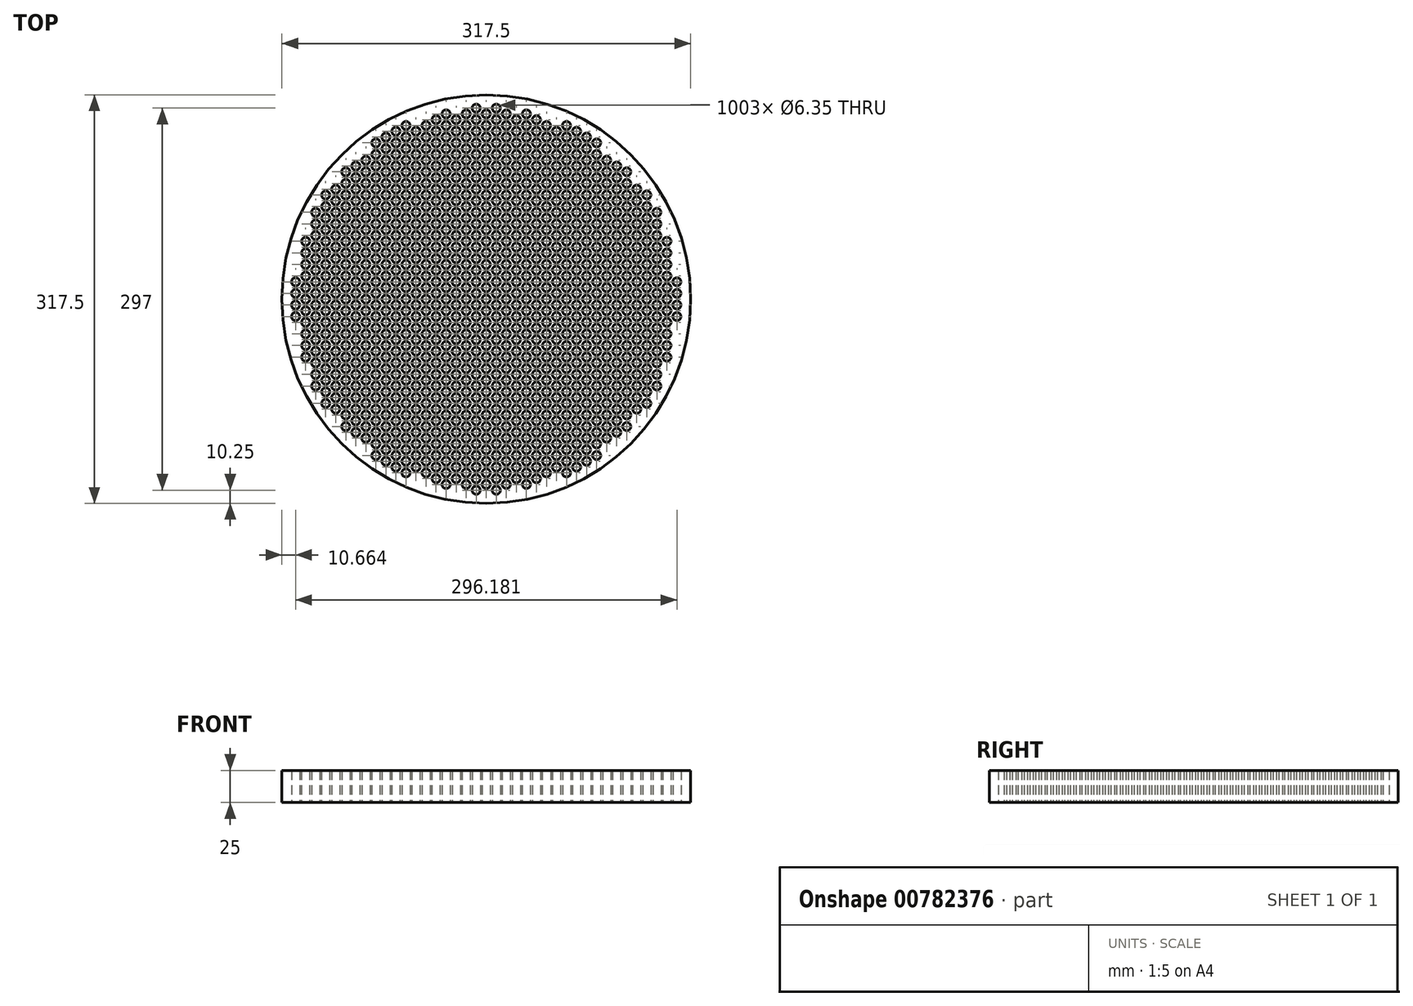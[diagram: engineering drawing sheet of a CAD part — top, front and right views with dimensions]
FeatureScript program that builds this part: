
annotation { "Feature Type Name" : "Feature", "Feature Type Description" : "" }
export const myFeature = defineFeature(function(context is Context, id is Id, definition is map)
    precondition{}
    {
        {
            var Q0;
            Q0=qCreatedBy(makeId("Top.planeOp"),FACE);
            var sketch = newSketch(context, id + "F0", { "sketchPlane" : qUnion([Q0])});
            skLineSegment(sketch, "E0.bottom", {"start": v(158.75, -158.75) * mm, "end": v(-158.75, -158.75) * mm});
            skLineSegment(sketch, "E0.top", {"start": v(158.75, 158.75) * mm, "end": v(-158.75, 158.75) * mm});
            skLineSegment(sketch, "E0.left", {"start": v(158.75, -158.75) * mm, "end": v(158.75, 158.75) * mm});
            skLineSegment(sketch, "E0.right", {"start": v(-158.75, -158.75) * mm, "end": v(-158.75, 158.75) * mm});
            skPoint(sketch, "E0.middle", {"position": v(0, 0) * mm});
            skCircle(sketch, "E1", {"center": v(-158.75, -158.75) * mm, "radius": 3.18 * mm});
            skCircle(sketch, "E2", {"center": v(-158.75, -149.75) * mm, "radius": 3.18 * mm});
            skCircle(sketch, "E3", {"center": v(-150.96, -154.25) * mm, "radius": 3.18 * mm});
            skCircle(sketch, "E4", {"center": v(-150.96, -145.25) * mm, "radius": 3.18 * mm});
            skCircle(sketch, "E5.0.1.0", {"center": v(-150.96, -127.25) * mm, "radius": 3.18 * mm});
            skCircle(sketch, "E5.0.1.1", {"center": v(-158.75, -140.75) * mm, "radius": 3.18 * mm});
            skCircle(sketch, "E5.0.1.2", {"center": v(-150.96, -136.25) * mm, "radius": 3.18 * mm});
            skCircle(sketch, "E5.0.1.3", {"center": v(-158.75, -131.75) * mm, "radius": 3.18 * mm});
            skCircle(sketch, "E5.0.2.0", {"center": v(-150.96, -109.25) * mm, "radius": 3.18 * mm});
            skCircle(sketch, "E5.0.2.1", {"center": v(-158.75, -122.75) * mm, "radius": 3.18 * mm});
            skCircle(sketch, "E5.0.2.2", {"center": v(-150.96, -118.25) * mm, "radius": 3.18 * mm});
            skCircle(sketch, "E5.0.2.3", {"center": v(-158.75, -113.75) * mm, "radius": 3.18 * mm});
            skCircle(sketch, "E5.0.3.0", {"center": v(-150.96, -91.25) * mm, "radius": 3.18 * mm});
            skCircle(sketch, "E5.0.3.1", {"center": v(-158.75, -104.75) * mm, "radius": 3.18 * mm});
            skCircle(sketch, "E5.0.3.2", {"center": v(-150.96, -100.25) * mm, "radius": 3.18 * mm});
            skCircle(sketch, "E5.0.3.3", {"center": v(-158.75, -95.75) * mm, "radius": 3.18 * mm});
            skCircle(sketch, "E5.0.4.0", {"center": v(-150.96, -73.25) * mm, "radius": 3.18 * mm});
            skCircle(sketch, "E5.0.4.1", {"center": v(-158.75, -86.75) * mm, "radius": 3.18 * mm});
            skCircle(sketch, "E5.0.4.2", {"center": v(-150.96, -82.25) * mm, "radius": 3.18 * mm});
            skCircle(sketch, "E5.0.4.3", {"center": v(-158.75, -77.75) * mm, "radius": 3.18 * mm});
            skCircle(sketch, "E5.0.5.0", {"center": v(-150.96, -55.25) * mm, "radius": 3.18 * mm});
            skCircle(sketch, "E5.0.5.1", {"center": v(-158.75, -68.75) * mm, "radius": 3.18 * mm});
            skCircle(sketch, "E5.0.5.2", {"center": v(-150.96, -64.25) * mm, "radius": 3.18 * mm});
            skCircle(sketch, "E5.0.5.3", {"center": v(-158.75, -59.75) * mm, "radius": 3.18 * mm});
            skCircle(sketch, "E5.0.6.0", {"center": v(-150.96, -37.25) * mm, "radius": 3.18 * mm});
            skCircle(sketch, "E5.0.6.1", {"center": v(-158.75, -50.75) * mm, "radius": 3.18 * mm});
            skCircle(sketch, "E5.0.6.2", {"center": v(-150.96, -46.25) * mm, "radius": 3.18 * mm});
            skCircle(sketch, "E5.0.6.3", {"center": v(-158.75, -41.75) * mm, "radius": 3.18 * mm});
            skCircle(sketch, "E5.0.7.0", {"center": v(-150.96, -19.25) * mm, "radius": 3.18 * mm});
            skCircle(sketch, "E5.0.7.1", {"center": v(-158.75, -32.75) * mm, "radius": 3.18 * mm});
            skCircle(sketch, "E5.0.7.2", {"center": v(-150.96, -28.25) * mm, "radius": 3.18 * mm});
            skCircle(sketch, "E5.0.7.3", {"center": v(-158.75, -23.75) * mm, "radius": 3.18 * mm});
            skCircle(sketch, "E5.0.8.0", {"center": v(-150.96, -1.25) * mm, "radius": 3.18 * mm});
            skCircle(sketch, "E5.0.8.1", {"center": v(-158.75, -14.75) * mm, "radius": 3.18 * mm});
            skCircle(sketch, "E5.0.8.2", {"center": v(-150.96, -10.25) * mm, "radius": 3.18 * mm});
            skCircle(sketch, "E5.0.8.3", {"center": v(-158.75, -5.75) * mm, "radius": 3.18 * mm});
            skCircle(sketch, "E5.0.9.0", {"center": v(-150.96, 16.75) * mm, "radius": 3.18 * mm});
            skCircle(sketch, "E5.0.9.1", {"center": v(-158.75, 3.25) * mm, "radius": 3.18 * mm});
            skCircle(sketch, "E5.0.9.2", {"center": v(-150.96, 7.75) * mm, "radius": 3.18 * mm});
            skCircle(sketch, "E5.0.9.3", {"center": v(-158.75, 12.25) * mm, "radius": 3.18 * mm});
            skCircle(sketch, "E5.0.10.0", {"center": v(-150.96, 34.75) * mm, "radius": 3.18 * mm});
            skCircle(sketch, "E5.0.10.1", {"center": v(-158.75, 21.25) * mm, "radius": 3.18 * mm});
            skCircle(sketch, "E5.0.10.2", {"center": v(-150.96, 25.75) * mm, "radius": 3.18 * mm});
            skCircle(sketch, "E5.0.10.3", {"center": v(-158.75, 30.25) * mm, "radius": 3.18 * mm});
            skCircle(sketch, "E5.0.11.0", {"center": v(-150.96, 52.75) * mm, "radius": 3.18 * mm});
            skCircle(sketch, "E5.0.11.1", {"center": v(-158.75, 39.25) * mm, "radius": 3.18 * mm});
            skCircle(sketch, "E5.0.11.2", {"center": v(-150.96, 43.75) * mm, "radius": 3.18 * mm});
            skCircle(sketch, "E5.0.11.3", {"center": v(-158.75, 48.25) * mm, "radius": 3.18 * mm});
            skCircle(sketch, "E5.0.12.0", {"center": v(-150.96, 70.75) * mm, "radius": 3.18 * mm});
            skCircle(sketch, "E5.0.12.1", {"center": v(-158.75, 57.25) * mm, "radius": 3.18 * mm});
            skCircle(sketch, "E5.0.12.2", {"center": v(-150.96, 61.75) * mm, "radius": 3.18 * mm});
            skCircle(sketch, "E5.0.12.3", {"center": v(-158.75, 66.25) * mm, "radius": 3.18 * mm});
            skCircle(sketch, "E5.0.13.0", {"center": v(-150.96, 88.75) * mm, "radius": 3.18 * mm});
            skCircle(sketch, "E5.0.13.1", {"center": v(-158.75, 75.25) * mm, "radius": 3.18 * mm});
            skCircle(sketch, "E5.0.13.2", {"center": v(-150.96, 79.75) * mm, "radius": 3.18 * mm});
            skCircle(sketch, "E5.0.13.3", {"center": v(-158.75, 84.25) * mm, "radius": 3.18 * mm});
            skCircle(sketch, "E5.0.14.0", {"center": v(-150.96, 106.75) * mm, "radius": 3.18 * mm});
            skCircle(sketch, "E5.0.14.1", {"center": v(-158.75, 93.25) * mm, "radius": 3.18 * mm});
            skCircle(sketch, "E5.0.14.2", {"center": v(-150.96, 97.75) * mm, "radius": 3.18 * mm});
            skCircle(sketch, "E5.0.14.3", {"center": v(-158.75, 102.25) * mm, "radius": 3.18 * mm});
            skCircle(sketch, "E5.0.15.0", {"center": v(-150.96, 124.75) * mm, "radius": 3.18 * mm});
            skCircle(sketch, "E5.0.15.1", {"center": v(-158.75, 111.25) * mm, "radius": 3.18 * mm});
            skCircle(sketch, "E5.0.15.2", {"center": v(-150.96, 115.75) * mm, "radius": 3.18 * mm});
            skCircle(sketch, "E5.0.15.3", {"center": v(-158.75, 120.25) * mm, "radius": 3.18 * mm});
            skCircle(sketch, "E5.0.16.0", {"center": v(-150.96, 142.75) * mm, "radius": 3.18 * mm});
            skCircle(sketch, "E5.0.16.1", {"center": v(-158.75, 129.25) * mm, "radius": 3.18 * mm});
            skCircle(sketch, "E5.0.16.2", {"center": v(-150.96, 133.75) * mm, "radius": 3.18 * mm});
            skCircle(sketch, "E5.0.16.3", {"center": v(-158.75, 138.25) * mm, "radius": 3.18 * mm});
            skCircle(sketch, "E5.0.17.0", {"center": v(-150.96, 160.75) * mm, "radius": 3.18 * mm});
            skCircle(sketch, "E5.0.17.1", {"center": v(-158.75, 147.25) * mm, "radius": 3.18 * mm});
            skCircle(sketch, "E5.0.17.2", {"center": v(-150.96, 151.75) * mm, "radius": 3.18 * mm});
            skCircle(sketch, "E5.0.17.3", {"center": v(-158.75, 156.25) * mm, "radius": 3.18 * mm});
            skCircle(sketch, "E5.1.0.0", {"center": v(-135.37, -145.25) * mm, "radius": 3.18 * mm});
            skCircle(sketch, "E5.1.0.1", {"center": v(-143.16, -158.75) * mm, "radius": 3.18 * mm});
            skCircle(sketch, "E5.1.0.2", {"center": v(-135.37, -154.25) * mm, "radius": 3.18 * mm});
            skCircle(sketch, "E5.1.0.3", {"center": v(-143.16, -149.75) * mm, "radius": 3.18 * mm});
            skCircle(sketch, "E5.1.1.0", {"center": v(-135.37, -127.25) * mm, "radius": 3.18 * mm});
            skCircle(sketch, "E5.1.1.1", {"center": v(-143.16, -140.75) * mm, "radius": 3.18 * mm});
            skCircle(sketch, "E5.1.1.2", {"center": v(-135.37, -136.25) * mm, "radius": 3.18 * mm});
            skCircle(sketch, "E5.1.1.3", {"center": v(-143.16, -131.75) * mm, "radius": 3.18 * mm});
            skCircle(sketch, "E5.1.2.0", {"center": v(-135.37, -109.25) * mm, "radius": 3.18 * mm});
            skCircle(sketch, "E5.1.2.1", {"center": v(-143.16, -122.75) * mm, "radius": 3.18 * mm});
            skCircle(sketch, "E5.1.2.2", {"center": v(-135.37, -118.25) * mm, "radius": 3.18 * mm});
            skCircle(sketch, "E5.1.2.3", {"center": v(-143.16, -113.75) * mm, "radius": 3.18 * mm});
            skCircle(sketch, "E5.1.3.0", {"center": v(-135.37, -91.25) * mm, "radius": 3.18 * mm});
            skCircle(sketch, "E5.1.3.1", {"center": v(-143.16, -104.75) * mm, "radius": 3.18 * mm});
            skCircle(sketch, "E5.1.3.2", {"center": v(-135.37, -100.25) * mm, "radius": 3.18 * mm});
            skCircle(sketch, "E5.1.3.3", {"center": v(-143.16, -95.75) * mm, "radius": 3.18 * mm});
            skCircle(sketch, "E5.1.4.0", {"center": v(-135.37, -73.25) * mm, "radius": 3.18 * mm});
            skCircle(sketch, "E5.1.4.1", {"center": v(-143.16, -86.75) * mm, "radius": 3.18 * mm});
            skCircle(sketch, "E5.1.4.2", {"center": v(-135.37, -82.25) * mm, "radius": 3.18 * mm});
            skCircle(sketch, "E5.1.4.3", {"center": v(-143.16, -77.75) * mm, "radius": 3.18 * mm});
            skCircle(sketch, "E5.1.5.0", {"center": v(-135.37, -55.25) * mm, "radius": 3.18 * mm});
            skCircle(sketch, "E5.1.5.1", {"center": v(-143.16, -68.75) * mm, "radius": 3.18 * mm});
            skCircle(sketch, "E5.1.5.2", {"center": v(-135.37, -64.25) * mm, "radius": 3.18 * mm});
            skCircle(sketch, "E5.1.5.3", {"center": v(-143.16, -59.75) * mm, "radius": 3.18 * mm});
            skCircle(sketch, "E5.1.6.0", {"center": v(-135.37, -37.25) * mm, "radius": 3.18 * mm});
            skCircle(sketch, "E5.1.6.1", {"center": v(-143.16, -50.75) * mm, "radius": 3.18 * mm});
            skCircle(sketch, "E5.1.6.2", {"center": v(-135.37, -46.25) * mm, "radius": 3.18 * mm});
            skCircle(sketch, "E5.1.6.3", {"center": v(-143.16, -41.75) * mm, "radius": 3.18 * mm});
            skCircle(sketch, "E5.1.7.0", {"center": v(-135.37, -19.25) * mm, "radius": 3.18 * mm});
            skCircle(sketch, "E5.1.7.1", {"center": v(-143.16, -32.75) * mm, "radius": 3.18 * mm});
            skCircle(sketch, "E5.1.7.2", {"center": v(-135.37, -28.25) * mm, "radius": 3.18 * mm});
            skCircle(sketch, "E5.1.7.3", {"center": v(-143.16, -23.75) * mm, "radius": 3.18 * mm});
            skCircle(sketch, "E5.1.8.0", {"center": v(-135.37, -1.25) * mm, "radius": 3.18 * mm});
            skCircle(sketch, "E5.1.8.1", {"center": v(-143.16, -14.75) * mm, "radius": 3.18 * mm});
            skCircle(sketch, "E5.1.8.2", {"center": v(-135.37, -10.25) * mm, "radius": 3.18 * mm});
            skCircle(sketch, "E5.1.8.3", {"center": v(-143.16, -5.75) * mm, "radius": 3.18 * mm});
            skCircle(sketch, "E5.1.9.0", {"center": v(-135.37, 16.75) * mm, "radius": 3.18 * mm});
            skCircle(sketch, "E5.1.9.1", {"center": v(-143.16, 3.25) * mm, "radius": 3.18 * mm});
            skCircle(sketch, "E5.1.9.2", {"center": v(-135.37, 7.75) * mm, "radius": 3.18 * mm});
            skCircle(sketch, "E5.1.9.3", {"center": v(-143.16, 12.25) * mm, "radius": 3.18 * mm});
            skCircle(sketch, "E5.1.10.0", {"center": v(-135.37, 34.75) * mm, "radius": 3.18 * mm});
            skCircle(sketch, "E5.1.10.1", {"center": v(-143.16, 21.25) * mm, "radius": 3.18 * mm});
            skCircle(sketch, "E5.1.10.2", {"center": v(-135.37, 25.75) * mm, "radius": 3.18 * mm});
            skCircle(sketch, "E5.1.10.3", {"center": v(-143.16, 30.25) * mm, "radius": 3.18 * mm});
            skCircle(sketch, "E5.1.11.0", {"center": v(-135.37, 52.75) * mm, "radius": 3.18 * mm});
            skCircle(sketch, "E5.1.11.1", {"center": v(-143.16, 39.25) * mm, "radius": 3.18 * mm});
            skCircle(sketch, "E5.1.11.2", {"center": v(-135.37, 43.75) * mm, "radius": 3.18 * mm});
            skCircle(sketch, "E5.1.11.3", {"center": v(-143.16, 48.25) * mm, "radius": 3.18 * mm});
            skCircle(sketch, "E5.1.12.0", {"center": v(-135.37, 70.75) * mm, "radius": 3.18 * mm});
            skCircle(sketch, "E5.1.12.1", {"center": v(-143.16, 57.25) * mm, "radius": 3.18 * mm});
            skCircle(sketch, "E5.1.12.2", {"center": v(-135.37, 61.75) * mm, "radius": 3.18 * mm});
            skCircle(sketch, "E5.1.12.3", {"center": v(-143.16, 66.25) * mm, "radius": 3.18 * mm});
            skCircle(sketch, "E5.1.13.0", {"center": v(-135.37, 88.75) * mm, "radius": 3.18 * mm});
            skCircle(sketch, "E5.1.13.1", {"center": v(-143.16, 75.25) * mm, "radius": 3.18 * mm});
            skCircle(sketch, "E5.1.13.2", {"center": v(-135.37, 79.75) * mm, "radius": 3.18 * mm});
            skCircle(sketch, "E5.1.13.3", {"center": v(-143.16, 84.25) * mm, "radius": 3.18 * mm});
            skCircle(sketch, "E5.1.14.0", {"center": v(-135.37, 106.75) * mm, "radius": 3.18 * mm});
            skCircle(sketch, "E5.1.14.1", {"center": v(-143.16, 93.25) * mm, "radius": 3.18 * mm});
            skCircle(sketch, "E5.1.14.2", {"center": v(-135.37, 97.75) * mm, "radius": 3.18 * mm});
            skCircle(sketch, "E5.1.14.3", {"center": v(-143.16, 102.25) * mm, "radius": 3.18 * mm});
            skCircle(sketch, "E5.1.15.0", {"center": v(-135.37, 124.75) * mm, "radius": 3.18 * mm});
            skCircle(sketch, "E5.1.15.1", {"center": v(-143.16, 111.25) * mm, "radius": 3.18 * mm});
            skCircle(sketch, "E5.1.15.2", {"center": v(-135.37, 115.75) * mm, "radius": 3.18 * mm});
            skCircle(sketch, "E5.1.15.3", {"center": v(-143.16, 120.25) * mm, "radius": 3.18 * mm});
            skCircle(sketch, "E5.1.16.0", {"center": v(-135.37, 142.75) * mm, "radius": 3.18 * mm});
            skCircle(sketch, "E5.1.16.1", {"center": v(-143.16, 129.25) * mm, "radius": 3.18 * mm});
            skCircle(sketch, "E5.1.16.2", {"center": v(-135.37, 133.75) * mm, "radius": 3.18 * mm});
            skCircle(sketch, "E5.1.16.3", {"center": v(-143.16, 138.25) * mm, "radius": 3.18 * mm});
            skCircle(sketch, "E5.1.17.0", {"center": v(-135.37, 160.75) * mm, "radius": 3.18 * mm});
            skCircle(sketch, "E5.1.17.1", {"center": v(-143.16, 147.25) * mm, "radius": 3.18 * mm});
            skCircle(sketch, "E5.1.17.2", {"center": v(-135.37, 151.75) * mm, "radius": 3.18 * mm});
            skCircle(sketch, "E5.1.17.3", {"center": v(-143.16, 156.25) * mm, "radius": 3.18 * mm});
            skCircle(sketch, "E5.2.0.0", {"center": v(-119.78, -145.25) * mm, "radius": 3.18 * mm});
            skCircle(sketch, "E5.2.0.1", {"center": v(-127.57, -158.75) * mm, "radius": 3.18 * mm});
            skCircle(sketch, "E5.2.0.2", {"center": v(-119.78, -154.25) * mm, "radius": 3.18 * mm});
            skCircle(sketch, "E5.2.0.3", {"center": v(-127.57, -149.75) * mm, "radius": 3.18 * mm});
            skCircle(sketch, "E5.2.1.0", {"center": v(-119.78, -127.25) * mm, "radius": 3.18 * mm});
            skCircle(sketch, "E5.2.1.1", {"center": v(-127.57, -140.75) * mm, "radius": 3.18 * mm});
            skCircle(sketch, "E5.2.1.2", {"center": v(-119.78, -136.25) * mm, "radius": 3.18 * mm});
            skCircle(sketch, "E5.2.1.3", {"center": v(-127.57, -131.75) * mm, "radius": 3.18 * mm});
            skCircle(sketch, "E5.2.2.0", {"center": v(-119.78, -109.25) * mm, "radius": 3.18 * mm});
            skCircle(sketch, "E5.2.2.1", {"center": v(-127.57, -122.75) * mm, "radius": 3.18 * mm});
            skCircle(sketch, "E5.2.2.2", {"center": v(-119.78, -118.25) * mm, "radius": 3.18 * mm});
            skCircle(sketch, "E5.2.2.3", {"center": v(-127.57, -113.75) * mm, "radius": 3.18 * mm});
            skCircle(sketch, "E5.2.3.0", {"center": v(-119.78, -91.25) * mm, "radius": 3.18 * mm});
            skCircle(sketch, "E5.2.3.1", {"center": v(-127.57, -104.75) * mm, "radius": 3.18 * mm});
            skCircle(sketch, "E5.2.3.2", {"center": v(-119.78, -100.25) * mm, "radius": 3.18 * mm});
            skCircle(sketch, "E5.2.3.3", {"center": v(-127.57, -95.75) * mm, "radius": 3.18 * mm});
            skCircle(sketch, "E5.2.4.0", {"center": v(-119.78, -73.25) * mm, "radius": 3.18 * mm});
            skCircle(sketch, "E5.2.4.1", {"center": v(-127.57, -86.75) * mm, "radius": 3.18 * mm});
            skCircle(sketch, "E5.2.4.2", {"center": v(-119.78, -82.25) * mm, "radius": 3.18 * mm});
            skCircle(sketch, "E5.2.4.3", {"center": v(-127.57, -77.75) * mm, "radius": 3.18 * mm});
            skCircle(sketch, "E5.2.5.0", {"center": v(-119.78, -55.25) * mm, "radius": 3.18 * mm});
            skCircle(sketch, "E5.2.5.1", {"center": v(-127.57, -68.75) * mm, "radius": 3.18 * mm});
            skCircle(sketch, "E5.2.5.2", {"center": v(-119.78, -64.25) * mm, "radius": 3.18 * mm});
            skCircle(sketch, "E5.2.5.3", {"center": v(-127.57, -59.75) * mm, "radius": 3.18 * mm});
            skCircle(sketch, "E5.2.6.0", {"center": v(-119.78, -37.25) * mm, "radius": 3.18 * mm});
            skCircle(sketch, "E5.2.6.1", {"center": v(-127.57, -50.75) * mm, "radius": 3.18 * mm});
            skCircle(sketch, "E5.2.6.2", {"center": v(-119.78, -46.25) * mm, "radius": 3.18 * mm});
            skCircle(sketch, "E5.2.6.3", {"center": v(-127.57, -41.75) * mm, "radius": 3.18 * mm});
            skCircle(sketch, "E5.2.7.0", {"center": v(-119.78, -19.25) * mm, "radius": 3.18 * mm});
            skCircle(sketch, "E5.2.7.1", {"center": v(-127.57, -32.75) * mm, "radius": 3.18 * mm});
            skCircle(sketch, "E5.2.7.2", {"center": v(-119.78, -28.25) * mm, "radius": 3.18 * mm});
            skCircle(sketch, "E5.2.7.3", {"center": v(-127.57, -23.75) * mm, "radius": 3.18 * mm});
            skCircle(sketch, "E5.2.8.0", {"center": v(-119.78, -1.25) * mm, "radius": 3.18 * mm});
            skCircle(sketch, "E5.2.8.1", {"center": v(-127.57, -14.75) * mm, "radius": 3.18 * mm});
            skCircle(sketch, "E5.2.8.2", {"center": v(-119.78, -10.25) * mm, "radius": 3.18 * mm});
            skCircle(sketch, "E5.2.8.3", {"center": v(-127.57, -5.75) * mm, "radius": 3.18 * mm});
            skCircle(sketch, "E5.2.9.0", {"center": v(-119.78, 16.75) * mm, "radius": 3.18 * mm});
            skCircle(sketch, "E5.2.9.1", {"center": v(-127.57, 3.25) * mm, "radius": 3.18 * mm});
            skCircle(sketch, "E5.2.9.2", {"center": v(-119.78, 7.75) * mm, "radius": 3.18 * mm});
            skCircle(sketch, "E5.2.9.3", {"center": v(-127.57, 12.25) * mm, "radius": 3.18 * mm});
            skCircle(sketch, "E5.2.10.0", {"center": v(-119.78, 34.75) * mm, "radius": 3.18 * mm});
            skCircle(sketch, "E5.2.10.1", {"center": v(-127.57, 21.25) * mm, "radius": 3.18 * mm});
            skCircle(sketch, "E5.2.10.2", {"center": v(-119.78, 25.75) * mm, "radius": 3.18 * mm});
            skCircle(sketch, "E5.2.10.3", {"center": v(-127.57, 30.25) * mm, "radius": 3.18 * mm});
            skCircle(sketch, "E5.2.11.0", {"center": v(-119.78, 52.75) * mm, "radius": 3.18 * mm});
            skCircle(sketch, "E5.2.11.1", {"center": v(-127.57, 39.25) * mm, "radius": 3.18 * mm});
            skCircle(sketch, "E5.2.11.2", {"center": v(-119.78, 43.75) * mm, "radius": 3.18 * mm});
            skCircle(sketch, "E5.2.11.3", {"center": v(-127.57, 48.25) * mm, "radius": 3.18 * mm});
            skCircle(sketch, "E5.2.12.0", {"center": v(-119.78, 70.75) * mm, "radius": 3.18 * mm});
            skCircle(sketch, "E5.2.12.1", {"center": v(-127.57, 57.25) * mm, "radius": 3.18 * mm});
            skCircle(sketch, "E5.2.12.2", {"center": v(-119.78, 61.75) * mm, "radius": 3.18 * mm});
            skCircle(sketch, "E5.2.12.3", {"center": v(-127.57, 66.25) * mm, "radius": 3.18 * mm});
            skCircle(sketch, "E5.2.13.0", {"center": v(-119.78, 88.75) * mm, "radius": 3.18 * mm});
            skCircle(sketch, "E5.2.13.1", {"center": v(-127.57, 75.25) * mm, "radius": 3.18 * mm});
            skCircle(sketch, "E5.2.13.2", {"center": v(-119.78, 79.75) * mm, "radius": 3.18 * mm});
            skCircle(sketch, "E5.2.13.3", {"center": v(-127.57, 84.25) * mm, "radius": 3.18 * mm});
            skCircle(sketch, "E5.2.14.0", {"center": v(-119.78, 106.75) * mm, "radius": 3.18 * mm});
            skCircle(sketch, "E5.2.14.1", {"center": v(-127.57, 93.25) * mm, "radius": 3.18 * mm});
            skCircle(sketch, "E5.2.14.2", {"center": v(-119.78, 97.75) * mm, "radius": 3.18 * mm});
            skCircle(sketch, "E5.2.14.3", {"center": v(-127.57, 102.25) * mm, "radius": 3.18 * mm});
            skCircle(sketch, "E5.2.15.0", {"center": v(-119.78, 124.75) * mm, "radius": 3.18 * mm});
            skCircle(sketch, "E5.2.15.1", {"center": v(-127.57, 111.25) * mm, "radius": 3.18 * mm});
            skCircle(sketch, "E5.2.15.2", {"center": v(-119.78, 115.75) * mm, "radius": 3.18 * mm});
            skCircle(sketch, "E5.2.15.3", {"center": v(-127.57, 120.25) * mm, "radius": 3.18 * mm});
            skCircle(sketch, "E5.2.16.0", {"center": v(-119.78, 142.75) * mm, "radius": 3.18 * mm});
            skCircle(sketch, "E5.2.16.1", {"center": v(-127.57, 129.25) * mm, "radius": 3.18 * mm});
            skCircle(sketch, "E5.2.16.2", {"center": v(-119.78, 133.75) * mm, "radius": 3.18 * mm});
            skCircle(sketch, "E5.2.16.3", {"center": v(-127.57, 138.25) * mm, "radius": 3.18 * mm});
            skCircle(sketch, "E5.2.17.0", {"center": v(-119.78, 160.75) * mm, "radius": 3.18 * mm});
            skCircle(sketch, "E5.2.17.1", {"center": v(-127.57, 147.25) * mm, "radius": 3.18 * mm});
            skCircle(sketch, "E5.2.17.2", {"center": v(-119.78, 151.75) * mm, "radius": 3.18 * mm});
            skCircle(sketch, "E5.2.17.3", {"center": v(-127.57, 156.25) * mm, "radius": 3.18 * mm});
            skCircle(sketch, "E5.3.0.0", {"center": v(-104.2, -145.25) * mm, "radius": 3.18 * mm});
            skCircle(sketch, "E5.3.0.1", {"center": v(-111.98, -158.75) * mm, "radius": 3.18 * mm});
            skCircle(sketch, "E5.3.0.2", {"center": v(-104.2, -154.25) * mm, "radius": 3.18 * mm});
            skCircle(sketch, "E5.3.0.3", {"center": v(-111.98, -149.75) * mm, "radius": 3.18 * mm});
            skCircle(sketch, "E5.3.1.0", {"center": v(-104.2, -127.25) * mm, "radius": 3.18 * mm});
            skCircle(sketch, "E5.3.1.1", {"center": v(-111.98, -140.75) * mm, "radius": 3.18 * mm});
            skCircle(sketch, "E5.3.1.2", {"center": v(-104.2, -136.25) * mm, "radius": 3.18 * mm});
            skCircle(sketch, "E5.3.1.3", {"center": v(-111.98, -131.75) * mm, "radius": 3.18 * mm});
            skCircle(sketch, "E5.3.2.0", {"center": v(-104.2, -109.25) * mm, "radius": 3.18 * mm});
            skCircle(sketch, "E5.3.2.1", {"center": v(-111.98, -122.75) * mm, "radius": 3.18 * mm});
            skCircle(sketch, "E5.3.2.2", {"center": v(-104.2, -118.25) * mm, "radius": 3.18 * mm});
            skCircle(sketch, "E5.3.2.3", {"center": v(-111.98, -113.75) * mm, "radius": 3.18 * mm});
            skCircle(sketch, "E5.3.3.0", {"center": v(-104.2, -91.25) * mm, "radius": 3.18 * mm});
            skCircle(sketch, "E5.3.3.1", {"center": v(-111.98, -104.75) * mm, "radius": 3.18 * mm});
            skCircle(sketch, "E5.3.3.2", {"center": v(-104.2, -100.25) * mm, "radius": 3.18 * mm});
            skCircle(sketch, "E5.3.3.3", {"center": v(-111.98, -95.75) * mm, "radius": 3.18 * mm});
            skCircle(sketch, "E5.3.4.0", {"center": v(-104.2, -73.25) * mm, "radius": 3.18 * mm});
            skCircle(sketch, "E5.3.4.1", {"center": v(-111.98, -86.75) * mm, "radius": 3.18 * mm});
            skCircle(sketch, "E5.3.4.2", {"center": v(-104.2, -82.25) * mm, "radius": 3.18 * mm});
            skCircle(sketch, "E5.3.4.3", {"center": v(-111.98, -77.75) * mm, "radius": 3.18 * mm});
            skCircle(sketch, "E5.3.5.0", {"center": v(-104.2, -55.25) * mm, "radius": 3.18 * mm});
            skCircle(sketch, "E5.3.5.1", {"center": v(-111.98, -68.75) * mm, "radius": 3.18 * mm});
            skCircle(sketch, "E5.3.5.2", {"center": v(-104.2, -64.25) * mm, "radius": 3.18 * mm});
            skCircle(sketch, "E5.3.5.3", {"center": v(-111.98, -59.75) * mm, "radius": 3.18 * mm});
            skCircle(sketch, "E5.3.6.0", {"center": v(-104.2, -37.25) * mm, "radius": 3.18 * mm});
            skCircle(sketch, "E5.3.6.1", {"center": v(-111.98, -50.75) * mm, "radius": 3.18 * mm});
            skCircle(sketch, "E5.3.6.2", {"center": v(-104.2, -46.25) * mm, "radius": 3.18 * mm});
            skCircle(sketch, "E5.3.6.3", {"center": v(-111.98, -41.75) * mm, "radius": 3.18 * mm});
            skCircle(sketch, "E5.3.7.0", {"center": v(-104.2, -19.25) * mm, "radius": 3.18 * mm});
            skCircle(sketch, "E5.3.7.1", {"center": v(-111.98, -32.75) * mm, "radius": 3.18 * mm});
            skCircle(sketch, "E5.3.7.2", {"center": v(-104.2, -28.25) * mm, "radius": 3.18 * mm});
            skCircle(sketch, "E5.3.7.3", {"center": v(-111.98, -23.75) * mm, "radius": 3.18 * mm});
            skCircle(sketch, "E5.3.8.0", {"center": v(-104.2, -1.25) * mm, "radius": 3.18 * mm});
            skCircle(sketch, "E5.3.8.1", {"center": v(-111.98, -14.75) * mm, "radius": 3.18 * mm});
            skCircle(sketch, "E5.3.8.2", {"center": v(-104.2, -10.25) * mm, "radius": 3.18 * mm});
            skCircle(sketch, "E5.3.8.3", {"center": v(-111.98, -5.75) * mm, "radius": 3.18 * mm});
            skCircle(sketch, "E5.3.9.0", {"center": v(-104.2, 16.75) * mm, "radius": 3.18 * mm});
            skCircle(sketch, "E5.3.9.1", {"center": v(-111.98, 3.25) * mm, "radius": 3.18 * mm});
            skCircle(sketch, "E5.3.9.2", {"center": v(-104.2, 7.75) * mm, "radius": 3.18 * mm});
            skCircle(sketch, "E5.3.9.3", {"center": v(-111.98, 12.25) * mm, "radius": 3.18 * mm});
            skCircle(sketch, "E5.3.10.0", {"center": v(-104.2, 34.75) * mm, "radius": 3.18 * mm});
            skCircle(sketch, "E5.3.10.1", {"center": v(-111.98, 21.25) * mm, "radius": 3.18 * mm});
            skCircle(sketch, "E5.3.10.2", {"center": v(-104.2, 25.75) * mm, "radius": 3.18 * mm});
            skCircle(sketch, "E5.3.10.3", {"center": v(-111.98, 30.25) * mm, "radius": 3.18 * mm});
            skCircle(sketch, "E5.3.11.0", {"center": v(-104.2, 52.75) * mm, "radius": 3.18 * mm});
            skCircle(sketch, "E5.3.11.1", {"center": v(-111.98, 39.25) * mm, "radius": 3.18 * mm});
            skCircle(sketch, "E5.3.11.2", {"center": v(-104.2, 43.75) * mm, "radius": 3.18 * mm});
            skCircle(sketch, "E5.3.11.3", {"center": v(-111.98, 48.25) * mm, "radius": 3.18 * mm});
            skCircle(sketch, "E5.3.12.0", {"center": v(-104.2, 70.75) * mm, "radius": 3.18 * mm});
            skCircle(sketch, "E5.3.12.1", {"center": v(-111.98, 57.25) * mm, "radius": 3.18 * mm});
            skCircle(sketch, "E5.3.12.2", {"center": v(-104.2, 61.75) * mm, "radius": 3.18 * mm});
            skCircle(sketch, "E5.3.12.3", {"center": v(-111.98, 66.25) * mm, "radius": 3.18 * mm});
            skCircle(sketch, "E5.3.13.0", {"center": v(-104.2, 88.75) * mm, "radius": 3.18 * mm});
            skCircle(sketch, "E5.3.13.1", {"center": v(-111.98, 75.25) * mm, "radius": 3.18 * mm});
            skCircle(sketch, "E5.3.13.2", {"center": v(-104.2, 79.75) * mm, "radius": 3.18 * mm});
            skCircle(sketch, "E5.3.13.3", {"center": v(-111.98, 84.25) * mm, "radius": 3.18 * mm});
            skCircle(sketch, "E5.3.14.0", {"center": v(-104.2, 106.75) * mm, "radius": 3.18 * mm});
            skCircle(sketch, "E5.3.14.1", {"center": v(-111.98, 93.25) * mm, "radius": 3.18 * mm});
            skCircle(sketch, "E5.3.14.2", {"center": v(-104.2, 97.75) * mm, "radius": 3.18 * mm});
            skCircle(sketch, "E5.3.14.3", {"center": v(-111.98, 102.25) * mm, "radius": 3.18 * mm});
            skCircle(sketch, "E5.3.15.0", {"center": v(-104.2, 124.75) * mm, "radius": 3.18 * mm});
            skCircle(sketch, "E5.3.15.1", {"center": v(-111.98, 111.25) * mm, "radius": 3.18 * mm});
            skCircle(sketch, "E5.3.15.2", {"center": v(-104.2, 115.75) * mm, "radius": 3.18 * mm});
            skCircle(sketch, "E5.3.15.3", {"center": v(-111.98, 120.25) * mm, "radius": 3.18 * mm});
            skCircle(sketch, "E5.3.16.0", {"center": v(-104.2, 142.75) * mm, "radius": 3.18 * mm});
            skCircle(sketch, "E5.3.16.1", {"center": v(-111.98, 129.25) * mm, "radius": 3.18 * mm});
            skCircle(sketch, "E5.3.16.2", {"center": v(-104.2, 133.75) * mm, "radius": 3.18 * mm});
            skCircle(sketch, "E5.3.16.3", {"center": v(-111.98, 138.25) * mm, "radius": 3.18 * mm});
            skCircle(sketch, "E5.3.17.0", {"center": v(-104.2, 160.75) * mm, "radius": 3.18 * mm});
            skCircle(sketch, "E5.3.17.1", {"center": v(-111.98, 147.25) * mm, "radius": 3.18 * mm});
            skCircle(sketch, "E5.3.17.2", {"center": v(-104.2, 151.75) * mm, "radius": 3.18 * mm});
            skCircle(sketch, "E5.3.17.3", {"center": v(-111.98, 156.25) * mm, "radius": 3.18 * mm});
            skCircle(sketch, "E5.4.0.0", {"center": v(-88.6, -145.25) * mm, "radius": 3.18 * mm});
            skCircle(sketch, "E5.4.0.1", {"center": v(-96.4, -158.75) * mm, "radius": 3.18 * mm});
            skCircle(sketch, "E5.4.0.2", {"center": v(-88.6, -154.25) * mm, "radius": 3.18 * mm});
            skCircle(sketch, "E5.4.0.3", {"center": v(-96.4, -149.75) * mm, "radius": 3.18 * mm});
            skCircle(sketch, "E5.4.1.0", {"center": v(-88.6, -127.25) * mm, "radius": 3.18 * mm});
            skCircle(sketch, "E5.4.1.1", {"center": v(-96.4, -140.75) * mm, "radius": 3.18 * mm});
            skCircle(sketch, "E5.4.1.2", {"center": v(-88.6, -136.25) * mm, "radius": 3.18 * mm});
            skCircle(sketch, "E5.4.1.3", {"center": v(-96.4, -131.75) * mm, "radius": 3.18 * mm});
            skCircle(sketch, "E5.4.2.0", {"center": v(-88.6, -109.25) * mm, "radius": 3.18 * mm});
            skCircle(sketch, "E5.4.2.1", {"center": v(-96.4, -122.75) * mm, "radius": 3.18 * mm});
            skCircle(sketch, "E5.4.2.2", {"center": v(-88.6, -118.25) * mm, "radius": 3.18 * mm});
            skCircle(sketch, "E5.4.2.3", {"center": v(-96.4, -113.75) * mm, "radius": 3.18 * mm});
            skCircle(sketch, "E5.4.3.0", {"center": v(-88.6, -91.25) * mm, "radius": 3.18 * mm});
            skCircle(sketch, "E5.4.3.1", {"center": v(-96.4, -104.75) * mm, "radius": 3.18 * mm});
            skCircle(sketch, "E5.4.3.2", {"center": v(-88.6, -100.25) * mm, "radius": 3.18 * mm});
            skCircle(sketch, "E5.4.3.3", {"center": v(-96.4, -95.75) * mm, "radius": 3.18 * mm});
            skCircle(sketch, "E5.4.4.0", {"center": v(-88.6, -73.25) * mm, "radius": 3.18 * mm});
            skCircle(sketch, "E5.4.4.1", {"center": v(-96.4, -86.75) * mm, "radius": 3.18 * mm});
            skCircle(sketch, "E5.4.4.2", {"center": v(-88.6, -82.25) * mm, "radius": 3.18 * mm});
            skCircle(sketch, "E5.4.4.3", {"center": v(-96.4, -77.75) * mm, "radius": 3.18 * mm});
            skCircle(sketch, "E5.4.5.0", {"center": v(-88.6, -55.25) * mm, "radius": 3.18 * mm});
            skCircle(sketch, "E5.4.5.1", {"center": v(-96.4, -68.75) * mm, "radius": 3.18 * mm});
            skCircle(sketch, "E5.4.5.2", {"center": v(-88.6, -64.25) * mm, "radius": 3.18 * mm});
            skCircle(sketch, "E5.4.5.3", {"center": v(-96.4, -59.75) * mm, "radius": 3.18 * mm});
            skCircle(sketch, "E5.4.6.0", {"center": v(-88.6, -37.25) * mm, "radius": 3.18 * mm});
            skCircle(sketch, "E5.4.6.1", {"center": v(-96.4, -50.75) * mm, "radius": 3.18 * mm});
            skCircle(sketch, "E5.4.6.2", {"center": v(-88.6, -46.25) * mm, "radius": 3.18 * mm});
            skCircle(sketch, "E5.4.6.3", {"center": v(-96.4, -41.75) * mm, "radius": 3.18 * mm});
            skCircle(sketch, "E5.4.7.0", {"center": v(-88.6, -19.25) * mm, "radius": 3.18 * mm});
            skCircle(sketch, "E5.4.7.1", {"center": v(-96.4, -32.75) * mm, "radius": 3.18 * mm});
            skCircle(sketch, "E5.4.7.2", {"center": v(-88.6, -28.25) * mm, "radius": 3.18 * mm});
            skCircle(sketch, "E5.4.7.3", {"center": v(-96.4, -23.75) * mm, "radius": 3.18 * mm});
            skCircle(sketch, "E5.4.8.0", {"center": v(-88.6, -1.25) * mm, "radius": 3.18 * mm});
            skCircle(sketch, "E5.4.8.1", {"center": v(-96.4, -14.75) * mm, "radius": 3.18 * mm});
            skCircle(sketch, "E5.4.8.2", {"center": v(-88.6, -10.25) * mm, "radius": 3.18 * mm});
            skCircle(sketch, "E5.4.8.3", {"center": v(-96.4, -5.75) * mm, "radius": 3.18 * mm});
            skCircle(sketch, "E5.4.9.0", {"center": v(-88.6, 16.75) * mm, "radius": 3.18 * mm});
            skCircle(sketch, "E5.4.9.1", {"center": v(-96.4, 3.25) * mm, "radius": 3.18 * mm});
            skCircle(sketch, "E5.4.9.2", {"center": v(-88.6, 7.75) * mm, "radius": 3.18 * mm});
            skCircle(sketch, "E5.4.9.3", {"center": v(-96.4, 12.25) * mm, "radius": 3.18 * mm});
            skCircle(sketch, "E5.4.10.0", {"center": v(-88.6, 34.75) * mm, "radius": 3.18 * mm});
            skCircle(sketch, "E5.4.10.1", {"center": v(-96.4, 21.25) * mm, "radius": 3.18 * mm});
            skCircle(sketch, "E5.4.10.2", {"center": v(-88.6, 25.75) * mm, "radius": 3.18 * mm});
            skCircle(sketch, "E5.4.10.3", {"center": v(-96.4, 30.25) * mm, "radius": 3.18 * mm});
            skCircle(sketch, "E5.4.11.0", {"center": v(-88.6, 52.75) * mm, "radius": 3.18 * mm});
            skCircle(sketch, "E5.4.11.1", {"center": v(-96.4, 39.25) * mm, "radius": 3.18 * mm});
            skCircle(sketch, "E5.4.11.2", {"center": v(-88.6, 43.75) * mm, "radius": 3.18 * mm});
            skCircle(sketch, "E5.4.11.3", {"center": v(-96.4, 48.25) * mm, "radius": 3.18 * mm});
            skCircle(sketch, "E5.4.12.0", {"center": v(-88.6, 70.75) * mm, "radius": 3.18 * mm});
            skCircle(sketch, "E5.4.12.1", {"center": v(-96.4, 57.25) * mm, "radius": 3.18 * mm});
            skCircle(sketch, "E5.4.12.2", {"center": v(-88.6, 61.75) * mm, "radius": 3.18 * mm});
            skCircle(sketch, "E5.4.12.3", {"center": v(-96.4, 66.25) * mm, "radius": 3.18 * mm});
            skCircle(sketch, "E5.4.13.0", {"center": v(-88.6, 88.75) * mm, "radius": 3.18 * mm});
            skCircle(sketch, "E5.4.13.1", {"center": v(-96.4, 75.25) * mm, "radius": 3.18 * mm});
            skCircle(sketch, "E5.4.13.2", {"center": v(-88.6, 79.75) * mm, "radius": 3.18 * mm});
            skCircle(sketch, "E5.4.13.3", {"center": v(-96.4, 84.25) * mm, "radius": 3.18 * mm});
            skCircle(sketch, "E5.4.14.0", {"center": v(-88.6, 106.75) * mm, "radius": 3.18 * mm});
            skCircle(sketch, "E5.4.14.1", {"center": v(-96.4, 93.25) * mm, "radius": 3.18 * mm});
            skCircle(sketch, "E5.4.14.2", {"center": v(-88.6, 97.75) * mm, "radius": 3.18 * mm});
            skCircle(sketch, "E5.4.14.3", {"center": v(-96.4, 102.25) * mm, "radius": 3.18 * mm});
            skCircle(sketch, "E5.4.15.0", {"center": v(-88.6, 124.75) * mm, "radius": 3.18 * mm});
            skCircle(sketch, "E5.4.15.1", {"center": v(-96.4, 111.25) * mm, "radius": 3.18 * mm});
            skCircle(sketch, "E5.4.15.2", {"center": v(-88.6, 115.75) * mm, "radius": 3.18 * mm});
            skCircle(sketch, "E5.4.15.3", {"center": v(-96.4, 120.25) * mm, "radius": 3.18 * mm});
            skCircle(sketch, "E5.4.16.0", {"center": v(-88.6, 142.75) * mm, "radius": 3.18 * mm});
            skCircle(sketch, "E5.4.16.1", {"center": v(-96.4, 129.25) * mm, "radius": 3.18 * mm});
            skCircle(sketch, "E5.4.16.2", {"center": v(-88.6, 133.75) * mm, "radius": 3.18 * mm});
            skCircle(sketch, "E5.4.16.3", {"center": v(-96.4, 138.25) * mm, "radius": 3.18 * mm});
            skCircle(sketch, "E5.4.17.0", {"center": v(-88.6, 160.75) * mm, "radius": 3.18 * mm});
            skCircle(sketch, "E5.4.17.1", {"center": v(-96.4, 147.25) * mm, "radius": 3.18 * mm});
            skCircle(sketch, "E5.4.17.2", {"center": v(-88.6, 151.75) * mm, "radius": 3.18 * mm});
            skCircle(sketch, "E5.4.17.3", {"center": v(-96.4, 156.25) * mm, "radius": 3.18 * mm});
            skCircle(sketch, "E5.5.0.0", {"center": v(-73.01, -145.25) * mm, "radius": 3.18 * mm});
            skCircle(sketch, "E5.5.0.1", {"center": v(-80.8, -158.75) * mm, "radius": 3.18 * mm});
            skCircle(sketch, "E5.5.0.2", {"center": v(-73.01, -154.25) * mm, "radius": 3.18 * mm});
            skCircle(sketch, "E5.5.0.3", {"center": v(-80.8, -149.75) * mm, "radius": 3.18 * mm});
            skCircle(sketch, "E5.5.1.0", {"center": v(-73.01, -127.25) * mm, "radius": 3.18 * mm});
            skCircle(sketch, "E5.5.1.1", {"center": v(-80.8, -140.75) * mm, "radius": 3.18 * mm});
            skCircle(sketch, "E5.5.1.2", {"center": v(-73.01, -136.25) * mm, "radius": 3.18 * mm});
            skCircle(sketch, "E5.5.1.3", {"center": v(-80.8, -131.75) * mm, "radius": 3.18 * mm});
            skCircle(sketch, "E5.5.2.0", {"center": v(-73.01, -109.25) * mm, "radius": 3.18 * mm});
            skCircle(sketch, "E5.5.2.1", {"center": v(-80.8, -122.75) * mm, "radius": 3.18 * mm});
            skCircle(sketch, "E5.5.2.2", {"center": v(-73.01, -118.25) * mm, "radius": 3.18 * mm});
            skCircle(sketch, "E5.5.2.3", {"center": v(-80.8, -113.75) * mm, "radius": 3.18 * mm});
            skCircle(sketch, "E5.5.3.0", {"center": v(-73.01, -91.25) * mm, "radius": 3.18 * mm});
            skCircle(sketch, "E5.5.3.1", {"center": v(-80.8, -104.75) * mm, "radius": 3.18 * mm});
            skCircle(sketch, "E5.5.3.2", {"center": v(-73.01, -100.25) * mm, "radius": 3.18 * mm});
            skCircle(sketch, "E5.5.3.3", {"center": v(-80.8, -95.75) * mm, "radius": 3.18 * mm});
            skCircle(sketch, "E5.5.4.0", {"center": v(-73.01, -73.25) * mm, "radius": 3.18 * mm});
            skCircle(sketch, "E5.5.4.1", {"center": v(-80.8, -86.75) * mm, "radius": 3.18 * mm});
            skCircle(sketch, "E5.5.4.2", {"center": v(-73.01, -82.25) * mm, "radius": 3.18 * mm});
            skCircle(sketch, "E5.5.4.3", {"center": v(-80.8, -77.75) * mm, "radius": 3.18 * mm});
            skCircle(sketch, "E5.5.5.0", {"center": v(-73.01, -55.25) * mm, "radius": 3.18 * mm});
            skCircle(sketch, "E5.5.5.1", {"center": v(-80.8, -68.75) * mm, "radius": 3.18 * mm});
            skCircle(sketch, "E5.5.5.2", {"center": v(-73.01, -64.25) * mm, "radius": 3.18 * mm});
            skCircle(sketch, "E5.5.5.3", {"center": v(-80.8, -59.75) * mm, "radius": 3.18 * mm});
            skCircle(sketch, "E5.5.6.0", {"center": v(-73.01, -37.25) * mm, "radius": 3.18 * mm});
            skCircle(sketch, "E5.5.6.1", {"center": v(-80.8, -50.75) * mm, "radius": 3.18 * mm});
            skCircle(sketch, "E5.5.6.2", {"center": v(-73.01, -46.25) * mm, "radius": 3.18 * mm});
            skCircle(sketch, "E5.5.6.3", {"center": v(-80.8, -41.75) * mm, "radius": 3.18 * mm});
            skCircle(sketch, "E5.5.7.0", {"center": v(-73.01, -19.25) * mm, "radius": 3.18 * mm});
            skCircle(sketch, "E5.5.7.1", {"center": v(-80.8, -32.75) * mm, "radius": 3.18 * mm});
            skCircle(sketch, "E5.5.7.2", {"center": v(-73.01, -28.25) * mm, "radius": 3.18 * mm});
            skCircle(sketch, "E5.5.7.3", {"center": v(-80.8, -23.75) * mm, "radius": 3.18 * mm});
            skCircle(sketch, "E5.5.8.0", {"center": v(-73.01, -1.25) * mm, "radius": 3.18 * mm});
            skCircle(sketch, "E5.5.8.1", {"center": v(-80.8, -14.75) * mm, "radius": 3.18 * mm});
            skCircle(sketch, "E5.5.8.2", {"center": v(-73.01, -10.25) * mm, "radius": 3.18 * mm});
            skCircle(sketch, "E5.5.8.3", {"center": v(-80.8, -5.75) * mm, "radius": 3.18 * mm});
            skCircle(sketch, "E5.5.9.0", {"center": v(-73.01, 16.75) * mm, "radius": 3.18 * mm});
            skCircle(sketch, "E5.5.9.1", {"center": v(-80.8, 3.25) * mm, "radius": 3.18 * mm});
            skCircle(sketch, "E5.5.9.2", {"center": v(-73.01, 7.75) * mm, "radius": 3.18 * mm});
            skCircle(sketch, "E5.5.9.3", {"center": v(-80.8, 12.25) * mm, "radius": 3.18 * mm});
            skCircle(sketch, "E5.5.10.0", {"center": v(-73.01, 34.75) * mm, "radius": 3.18 * mm});
            skCircle(sketch, "E5.5.10.1", {"center": v(-80.8, 21.25) * mm, "radius": 3.18 * mm});
            skCircle(sketch, "E5.5.10.2", {"center": v(-73.01, 25.75) * mm, "radius": 3.18 * mm});
            skCircle(sketch, "E5.5.10.3", {"center": v(-80.8, 30.25) * mm, "radius": 3.18 * mm});
            skCircle(sketch, "E5.5.11.0", {"center": v(-73.01, 52.75) * mm, "radius": 3.18 * mm});
            skCircle(sketch, "E5.5.11.1", {"center": v(-80.8, 39.25) * mm, "radius": 3.18 * mm});
            skCircle(sketch, "E5.5.11.2", {"center": v(-73.01, 43.75) * mm, "radius": 3.18 * mm});
            skCircle(sketch, "E5.5.11.3", {"center": v(-80.8, 48.25) * mm, "radius": 3.18 * mm});
            skCircle(sketch, "E5.5.12.0", {"center": v(-73.01, 70.75) * mm, "radius": 3.18 * mm});
            skCircle(sketch, "E5.5.12.1", {"center": v(-80.8, 57.25) * mm, "radius": 3.18 * mm});
            skCircle(sketch, "E5.5.12.2", {"center": v(-73.01, 61.75) * mm, "radius": 3.18 * mm});
            skCircle(sketch, "E5.5.12.3", {"center": v(-80.8, 66.25) * mm, "radius": 3.18 * mm});
            skCircle(sketch, "E5.5.13.0", {"center": v(-73.01, 88.75) * mm, "radius": 3.18 * mm});
            skCircle(sketch, "E5.5.13.1", {"center": v(-80.8, 75.25) * mm, "radius": 3.18 * mm});
            skCircle(sketch, "E5.5.13.2", {"center": v(-73.01, 79.75) * mm, "radius": 3.18 * mm});
            skCircle(sketch, "E5.5.13.3", {"center": v(-80.8, 84.25) * mm, "radius": 3.18 * mm});
            skCircle(sketch, "E5.5.14.0", {"center": v(-73.01, 106.75) * mm, "radius": 3.18 * mm});
            skCircle(sketch, "E5.5.14.1", {"center": v(-80.8, 93.25) * mm, "radius": 3.18 * mm});
            skCircle(sketch, "E5.5.14.2", {"center": v(-73.01, 97.75) * mm, "radius": 3.18 * mm});
            skCircle(sketch, "E5.5.14.3", {"center": v(-80.8, 102.25) * mm, "radius": 3.18 * mm});
            skCircle(sketch, "E5.5.15.0", {"center": v(-73.01, 124.75) * mm, "radius": 3.18 * mm});
            skCircle(sketch, "E5.5.15.1", {"center": v(-80.8, 111.25) * mm, "radius": 3.18 * mm});
            skCircle(sketch, "E5.5.15.2", {"center": v(-73.01, 115.75) * mm, "radius": 3.18 * mm});
            skCircle(sketch, "E5.5.15.3", {"center": v(-80.8, 120.25) * mm, "radius": 3.18 * mm});
            skCircle(sketch, "E5.5.16.0", {"center": v(-73.01, 142.75) * mm, "radius": 3.18 * mm});
            skCircle(sketch, "E5.5.16.1", {"center": v(-80.8, 129.25) * mm, "radius": 3.18 * mm});
            skCircle(sketch, "E5.5.16.2", {"center": v(-73.01, 133.75) * mm, "radius": 3.18 * mm});
            skCircle(sketch, "E5.5.16.3", {"center": v(-80.8, 138.25) * mm, "radius": 3.18 * mm});
            skCircle(sketch, "E5.5.17.0", {"center": v(-73.01, 160.75) * mm, "radius": 3.18 * mm});
            skCircle(sketch, "E5.5.17.1", {"center": v(-80.8, 147.25) * mm, "radius": 3.18 * mm});
            skCircle(sketch, "E5.5.17.2", {"center": v(-73.01, 151.75) * mm, "radius": 3.18 * mm});
            skCircle(sketch, "E5.5.17.3", {"center": v(-80.8, 156.25) * mm, "radius": 3.18 * mm});
            skCircle(sketch, "E5.6.0.0", {"center": v(-57.43, -145.25) * mm, "radius": 3.18 * mm});
            skCircle(sketch, "E5.6.0.1", {"center": v(-65.22, -158.75) * mm, "radius": 3.18 * mm});
            skCircle(sketch, "E5.6.0.2", {"center": v(-57.43, -154.25) * mm, "radius": 3.18 * mm});
            skCircle(sketch, "E5.6.0.3", {"center": v(-65.22, -149.75) * mm, "radius": 3.18 * mm});
            skCircle(sketch, "E5.6.1.0", {"center": v(-57.43, -127.25) * mm, "radius": 3.18 * mm});
            skCircle(sketch, "E5.6.1.1", {"center": v(-65.22, -140.75) * mm, "radius": 3.18 * mm});
            skCircle(sketch, "E5.6.1.2", {"center": v(-57.43, -136.25) * mm, "radius": 3.18 * mm});
            skCircle(sketch, "E5.6.1.3", {"center": v(-65.22, -131.75) * mm, "radius": 3.18 * mm});
            skCircle(sketch, "E5.6.2.0", {"center": v(-57.43, -109.25) * mm, "radius": 3.18 * mm});
            skCircle(sketch, "E5.6.2.1", {"center": v(-65.22, -122.75) * mm, "radius": 3.18 * mm});
            skCircle(sketch, "E5.6.2.2", {"center": v(-57.43, -118.25) * mm, "radius": 3.18 * mm});
            skCircle(sketch, "E5.6.2.3", {"center": v(-65.22, -113.75) * mm, "radius": 3.18 * mm});
            skCircle(sketch, "E5.6.3.0", {"center": v(-57.43, -91.25) * mm, "radius": 3.18 * mm});
            skCircle(sketch, "E5.6.3.1", {"center": v(-65.22, -104.75) * mm, "radius": 3.18 * mm});
            skCircle(sketch, "E5.6.3.2", {"center": v(-57.43, -100.25) * mm, "radius": 3.18 * mm});
            skCircle(sketch, "E5.6.3.3", {"center": v(-65.22, -95.75) * mm, "radius": 3.18 * mm});
            skCircle(sketch, "E5.6.4.0", {"center": v(-57.43, -73.25) * mm, "radius": 3.18 * mm});
            skCircle(sketch, "E5.6.4.1", {"center": v(-65.22, -86.75) * mm, "radius": 3.18 * mm});
            skCircle(sketch, "E5.6.4.2", {"center": v(-57.43, -82.25) * mm, "radius": 3.18 * mm});
            skCircle(sketch, "E5.6.4.3", {"center": v(-65.22, -77.75) * mm, "radius": 3.18 * mm});
            skCircle(sketch, "E5.6.5.0", {"center": v(-57.43, -55.25) * mm, "radius": 3.18 * mm});
            skCircle(sketch, "E5.6.5.1", {"center": v(-65.22, -68.75) * mm, "radius": 3.18 * mm});
            skCircle(sketch, "E5.6.5.2", {"center": v(-57.43, -64.25) * mm, "radius": 3.18 * mm});
            skCircle(sketch, "E5.6.5.3", {"center": v(-65.22, -59.75) * mm, "radius": 3.18 * mm});
            skCircle(sketch, "E5.6.6.0", {"center": v(-57.43, -37.25) * mm, "radius": 3.18 * mm});
            skCircle(sketch, "E5.6.6.1", {"center": v(-65.22, -50.75) * mm, "radius": 3.18 * mm});
            skCircle(sketch, "E5.6.6.2", {"center": v(-57.43, -46.25) * mm, "radius": 3.18 * mm});
            skCircle(sketch, "E5.6.6.3", {"center": v(-65.22, -41.75) * mm, "radius": 3.18 * mm});
            skCircle(sketch, "E5.6.7.0", {"center": v(-57.43, -19.25) * mm, "radius": 3.18 * mm});
            skCircle(sketch, "E5.6.7.1", {"center": v(-65.22, -32.75) * mm, "radius": 3.18 * mm});
            skCircle(sketch, "E5.6.7.2", {"center": v(-57.43, -28.25) * mm, "radius": 3.18 * mm});
            skCircle(sketch, "E5.6.7.3", {"center": v(-65.22, -23.75) * mm, "radius": 3.18 * mm});
            skCircle(sketch, "E5.6.8.0", {"center": v(-57.43, -1.25) * mm, "radius": 3.18 * mm});
            skCircle(sketch, "E5.6.8.1", {"center": v(-65.22, -14.75) * mm, "radius": 3.18 * mm});
            skCircle(sketch, "E5.6.8.2", {"center": v(-57.43, -10.25) * mm, "radius": 3.18 * mm});
            skCircle(sketch, "E5.6.8.3", {"center": v(-65.22, -5.75) * mm, "radius": 3.18 * mm});
            skCircle(sketch, "E5.6.9.0", {"center": v(-57.43, 16.75) * mm, "radius": 3.18 * mm});
            skCircle(sketch, "E5.6.9.1", {"center": v(-65.22, 3.25) * mm, "radius": 3.18 * mm});
            skCircle(sketch, "E5.6.9.2", {"center": v(-57.43, 7.75) * mm, "radius": 3.18 * mm});
            skCircle(sketch, "E5.6.9.3", {"center": v(-65.22, 12.25) * mm, "radius": 3.18 * mm});
            skCircle(sketch, "E5.6.10.0", {"center": v(-57.43, 34.75) * mm, "radius": 3.18 * mm});
            skCircle(sketch, "E5.6.10.1", {"center": v(-65.22, 21.25) * mm, "radius": 3.18 * mm});
            skCircle(sketch, "E5.6.10.2", {"center": v(-57.43, 25.75) * mm, "radius": 3.18 * mm});
            skCircle(sketch, "E5.6.10.3", {"center": v(-65.22, 30.25) * mm, "radius": 3.18 * mm});
            skCircle(sketch, "E5.6.11.0", {"center": v(-57.43, 52.75) * mm, "radius": 3.18 * mm});
            skCircle(sketch, "E5.6.11.1", {"center": v(-65.22, 39.25) * mm, "radius": 3.18 * mm});
            skCircle(sketch, "E5.6.11.2", {"center": v(-57.43, 43.75) * mm, "radius": 3.18 * mm});
            skCircle(sketch, "E5.6.11.3", {"center": v(-65.22, 48.25) * mm, "radius": 3.18 * mm});
            skCircle(sketch, "E5.6.12.0", {"center": v(-57.43, 70.75) * mm, "radius": 3.18 * mm});
            skCircle(sketch, "E5.6.12.1", {"center": v(-65.22, 57.25) * mm, "radius": 3.18 * mm});
            skCircle(sketch, "E5.6.12.2", {"center": v(-57.43, 61.75) * mm, "radius": 3.18 * mm});
            skCircle(sketch, "E5.6.12.3", {"center": v(-65.22, 66.25) * mm, "radius": 3.18 * mm});
            skCircle(sketch, "E5.6.13.0", {"center": v(-57.43, 88.75) * mm, "radius": 3.18 * mm});
            skCircle(sketch, "E5.6.13.1", {"center": v(-65.22, 75.25) * mm, "radius": 3.18 * mm});
            skCircle(sketch, "E5.6.13.2", {"center": v(-57.43, 79.75) * mm, "radius": 3.18 * mm});
            skCircle(sketch, "E5.6.13.3", {"center": v(-65.22, 84.25) * mm, "radius": 3.18 * mm});
            skCircle(sketch, "E5.6.14.0", {"center": v(-57.43, 106.75) * mm, "radius": 3.18 * mm});
            skCircle(sketch, "E5.6.14.1", {"center": v(-65.22, 93.25) * mm, "radius": 3.18 * mm});
            skCircle(sketch, "E5.6.14.2", {"center": v(-57.43, 97.75) * mm, "radius": 3.18 * mm});
            skCircle(sketch, "E5.6.14.3", {"center": v(-65.22, 102.25) * mm, "radius": 3.18 * mm});
            skCircle(sketch, "E5.6.15.0", {"center": v(-57.43, 124.75) * mm, "radius": 3.18 * mm});
            skCircle(sketch, "E5.6.15.1", {"center": v(-65.22, 111.25) * mm, "radius": 3.18 * mm});
            skCircle(sketch, "E5.6.15.2", {"center": v(-57.43, 115.75) * mm, "radius": 3.18 * mm});
            skCircle(sketch, "E5.6.15.3", {"center": v(-65.22, 120.25) * mm, "radius": 3.18 * mm});
            skCircle(sketch, "E5.6.16.0", {"center": v(-57.43, 142.75) * mm, "radius": 3.18 * mm});
            skCircle(sketch, "E5.6.16.1", {"center": v(-65.22, 129.25) * mm, "radius": 3.18 * mm});
            skCircle(sketch, "E5.6.16.2", {"center": v(-57.43, 133.75) * mm, "radius": 3.18 * mm});
            skCircle(sketch, "E5.6.16.3", {"center": v(-65.22, 138.25) * mm, "radius": 3.18 * mm});
            skCircle(sketch, "E5.6.17.0", {"center": v(-57.43, 160.75) * mm, "radius": 3.18 * mm});
            skCircle(sketch, "E5.6.17.1", {"center": v(-65.22, 147.25) * mm, "radius": 3.18 * mm});
            skCircle(sketch, "E5.6.17.2", {"center": v(-57.43, 151.75) * mm, "radius": 3.18 * mm});
            skCircle(sketch, "E5.6.17.3", {"center": v(-65.22, 156.25) * mm, "radius": 3.18 * mm});
            skCircle(sketch, "E5.7.0.0", {"center": v(-41.84, -145.25) * mm, "radius": 3.18 * mm});
            skCircle(sketch, "E5.7.0.1", {"center": v(-49.63, -158.75) * mm, "radius": 3.18 * mm});
            skCircle(sketch, "E5.7.0.2", {"center": v(-41.84, -154.25) * mm, "radius": 3.18 * mm});
            skCircle(sketch, "E5.7.0.3", {"center": v(-49.63, -149.75) * mm, "radius": 3.18 * mm});
            skCircle(sketch, "E5.7.1.0", {"center": v(-41.84, -127.25) * mm, "radius": 3.18 * mm});
            skCircle(sketch, "E5.7.1.1", {"center": v(-49.63, -140.75) * mm, "radius": 3.18 * mm});
            skCircle(sketch, "E5.7.1.2", {"center": v(-41.84, -136.25) * mm, "radius": 3.18 * mm});
            skCircle(sketch, "E5.7.1.3", {"center": v(-49.63, -131.75) * mm, "radius": 3.18 * mm});
            skCircle(sketch, "E5.7.2.0", {"center": v(-41.84, -109.25) * mm, "radius": 3.18 * mm});
            skCircle(sketch, "E5.7.2.1", {"center": v(-49.63, -122.75) * mm, "radius": 3.18 * mm});
            skCircle(sketch, "E5.7.2.2", {"center": v(-41.84, -118.25) * mm, "radius": 3.18 * mm});
            skCircle(sketch, "E5.7.2.3", {"center": v(-49.63, -113.75) * mm, "radius": 3.18 * mm});
            skCircle(sketch, "E5.7.3.0", {"center": v(-41.84, -91.25) * mm, "radius": 3.18 * mm});
            skCircle(sketch, "E5.7.3.1", {"center": v(-49.63, -104.75) * mm, "radius": 3.18 * mm});
            skCircle(sketch, "E5.7.3.2", {"center": v(-41.84, -100.25) * mm, "radius": 3.18 * mm});
            skCircle(sketch, "E5.7.3.3", {"center": v(-49.63, -95.75) * mm, "radius": 3.18 * mm});
            skCircle(sketch, "E5.7.4.0", {"center": v(-41.84, -73.25) * mm, "radius": 3.18 * mm});
            skCircle(sketch, "E5.7.4.1", {"center": v(-49.63, -86.75) * mm, "radius": 3.18 * mm});
            skCircle(sketch, "E5.7.4.2", {"center": v(-41.84, -82.25) * mm, "radius": 3.18 * mm});
            skCircle(sketch, "E5.7.4.3", {"center": v(-49.63, -77.75) * mm, "radius": 3.18 * mm});
            skCircle(sketch, "E5.7.5.0", {"center": v(-41.84, -55.25) * mm, "radius": 3.18 * mm});
            skCircle(sketch, "E5.7.5.1", {"center": v(-49.63, -68.75) * mm, "radius": 3.18 * mm});
            skCircle(sketch, "E5.7.5.2", {"center": v(-41.84, -64.25) * mm, "radius": 3.18 * mm});
            skCircle(sketch, "E5.7.5.3", {"center": v(-49.63, -59.75) * mm, "radius": 3.18 * mm});
            skCircle(sketch, "E5.7.6.0", {"center": v(-41.84, -37.25) * mm, "radius": 3.18 * mm});
            skCircle(sketch, "E5.7.6.1", {"center": v(-49.63, -50.75) * mm, "radius": 3.18 * mm});
            skCircle(sketch, "E5.7.6.2", {"center": v(-41.84, -46.25) * mm, "radius": 3.18 * mm});
            skCircle(sketch, "E5.7.6.3", {"center": v(-49.63, -41.75) * mm, "radius": 3.18 * mm});
            skCircle(sketch, "E5.7.7.0", {"center": v(-41.84, -19.25) * mm, "radius": 3.18 * mm});
            skCircle(sketch, "E5.7.7.1", {"center": v(-49.63, -32.75) * mm, "radius": 3.18 * mm});
            skCircle(sketch, "E5.7.7.2", {"center": v(-41.84, -28.25) * mm, "radius": 3.18 * mm});
            skCircle(sketch, "E5.7.7.3", {"center": v(-49.63, -23.75) * mm, "radius": 3.18 * mm});
            skCircle(sketch, "E5.7.8.0", {"center": v(-41.84, -1.25) * mm, "radius": 3.18 * mm});
            skCircle(sketch, "E5.7.8.1", {"center": v(-49.63, -14.75) * mm, "radius": 3.18 * mm});
            skCircle(sketch, "E5.7.8.2", {"center": v(-41.84, -10.25) * mm, "radius": 3.18 * mm});
            skCircle(sketch, "E5.7.8.3", {"center": v(-49.63, -5.75) * mm, "radius": 3.18 * mm});
            skCircle(sketch, "E5.7.9.0", {"center": v(-41.84, 16.75) * mm, "radius": 3.18 * mm});
            skCircle(sketch, "E5.7.9.1", {"center": v(-49.63, 3.25) * mm, "radius": 3.18 * mm});
            skCircle(sketch, "E5.7.9.2", {"center": v(-41.84, 7.75) * mm, "radius": 3.18 * mm});
            skCircle(sketch, "E5.7.9.3", {"center": v(-49.63, 12.25) * mm, "radius": 3.18 * mm});
            skCircle(sketch, "E5.7.10.0", {"center": v(-41.84, 34.75) * mm, "radius": 3.18 * mm});
            skCircle(sketch, "E5.7.10.1", {"center": v(-49.63, 21.25) * mm, "radius": 3.18 * mm});
            skCircle(sketch, "E5.7.10.2", {"center": v(-41.84, 25.75) * mm, "radius": 3.18 * mm});
            skCircle(sketch, "E5.7.10.3", {"center": v(-49.63, 30.25) * mm, "radius": 3.18 * mm});
            skCircle(sketch, "E5.7.11.0", {"center": v(-41.84, 52.75) * mm, "radius": 3.18 * mm});
            skCircle(sketch, "E5.7.11.1", {"center": v(-49.63, 39.25) * mm, "radius": 3.18 * mm});
            skCircle(sketch, "E5.7.11.2", {"center": v(-41.84, 43.75) * mm, "radius": 3.18 * mm});
            skCircle(sketch, "E5.7.11.3", {"center": v(-49.63, 48.25) * mm, "radius": 3.18 * mm});
            skCircle(sketch, "E5.7.12.0", {"center": v(-41.84, 70.75) * mm, "radius": 3.18 * mm});
            skCircle(sketch, "E5.7.12.1", {"center": v(-49.63, 57.25) * mm, "radius": 3.18 * mm});
            skCircle(sketch, "E5.7.12.2", {"center": v(-41.84, 61.75) * mm, "radius": 3.18 * mm});
            skCircle(sketch, "E5.7.12.3", {"center": v(-49.63, 66.25) * mm, "radius": 3.18 * mm});
            skCircle(sketch, "E5.7.13.0", {"center": v(-41.84, 88.75) * mm, "radius": 3.18 * mm});
            skCircle(sketch, "E5.7.13.1", {"center": v(-49.63, 75.25) * mm, "radius": 3.18 * mm});
            skCircle(sketch, "E5.7.13.2", {"center": v(-41.84, 79.75) * mm, "radius": 3.18 * mm});
            skCircle(sketch, "E5.7.13.3", {"center": v(-49.63, 84.25) * mm, "radius": 3.18 * mm});
            skCircle(sketch, "E5.7.14.0", {"center": v(-41.84, 106.75) * mm, "radius": 3.18 * mm});
            skCircle(sketch, "E5.7.14.1", {"center": v(-49.63, 93.25) * mm, "radius": 3.18 * mm});
            skCircle(sketch, "E5.7.14.2", {"center": v(-41.84, 97.75) * mm, "radius": 3.18 * mm});
            skCircle(sketch, "E5.7.14.3", {"center": v(-49.63, 102.25) * mm, "radius": 3.18 * mm});
            skCircle(sketch, "E5.7.15.0", {"center": v(-41.84, 124.75) * mm, "radius": 3.18 * mm});
            skCircle(sketch, "E5.7.15.1", {"center": v(-49.63, 111.25) * mm, "radius": 3.18 * mm});
            skCircle(sketch, "E5.7.15.2", {"center": v(-41.84, 115.75) * mm, "radius": 3.18 * mm});
            skCircle(sketch, "E5.7.15.3", {"center": v(-49.63, 120.25) * mm, "radius": 3.18 * mm});
            skCircle(sketch, "E5.7.16.0", {"center": v(-41.84, 142.75) * mm, "radius": 3.18 * mm});
            skCircle(sketch, "E5.7.16.1", {"center": v(-49.63, 129.25) * mm, "radius": 3.18 * mm});
            skCircle(sketch, "E5.7.16.2", {"center": v(-41.84, 133.75) * mm, "radius": 3.18 * mm});
            skCircle(sketch, "E5.7.16.3", {"center": v(-49.63, 138.25) * mm, "radius": 3.18 * mm});
            skCircle(sketch, "E5.7.17.0", {"center": v(-41.84, 160.75) * mm, "radius": 3.18 * mm});
            skCircle(sketch, "E5.7.17.1", {"center": v(-49.63, 147.25) * mm, "radius": 3.18 * mm});
            skCircle(sketch, "E5.7.17.2", {"center": v(-41.84, 151.75) * mm, "radius": 3.18 * mm});
            skCircle(sketch, "E5.7.17.3", {"center": v(-49.63, 156.25) * mm, "radius": 3.18 * mm});
            skCircle(sketch, "E5.8.0.0", {"center": v(-26.25, -145.25) * mm, "radius": 3.18 * mm});
            skCircle(sketch, "E5.8.0.1", {"center": v(-34.04, -158.75) * mm, "radius": 3.18 * mm});
            skCircle(sketch, "E5.8.0.2", {"center": v(-26.25, -154.25) * mm, "radius": 3.18 * mm});
            skCircle(sketch, "E5.8.0.3", {"center": v(-34.04, -149.75) * mm, "radius": 3.18 * mm});
            skCircle(sketch, "E5.8.1.0", {"center": v(-26.25, -127.25) * mm, "radius": 3.18 * mm});
            skCircle(sketch, "E5.8.1.1", {"center": v(-34.04, -140.75) * mm, "radius": 3.18 * mm});
            skCircle(sketch, "E5.8.1.2", {"center": v(-26.25, -136.25) * mm, "radius": 3.18 * mm});
            skCircle(sketch, "E5.8.1.3", {"center": v(-34.04, -131.75) * mm, "radius": 3.18 * mm});
            skCircle(sketch, "E5.8.2.0", {"center": v(-26.25, -109.25) * mm, "radius": 3.18 * mm});
            skCircle(sketch, "E5.8.2.1", {"center": v(-34.04, -122.75) * mm, "radius": 3.18 * mm});
            skCircle(sketch, "E5.8.2.2", {"center": v(-26.25, -118.25) * mm, "radius": 3.18 * mm});
            skCircle(sketch, "E5.8.2.3", {"center": v(-34.04, -113.75) * mm, "radius": 3.18 * mm});
            skCircle(sketch, "E5.8.3.0", {"center": v(-26.25, -91.25) * mm, "radius": 3.18 * mm});
            skCircle(sketch, "E5.8.3.1", {"center": v(-34.04, -104.75) * mm, "radius": 3.18 * mm});
            skCircle(sketch, "E5.8.3.2", {"center": v(-26.25, -100.25) * mm, "radius": 3.18 * mm});
            skCircle(sketch, "E5.8.3.3", {"center": v(-34.04, -95.75) * mm, "radius": 3.18 * mm});
            skCircle(sketch, "E5.8.4.0", {"center": v(-26.25, -73.25) * mm, "radius": 3.18 * mm});
            skCircle(sketch, "E5.8.4.1", {"center": v(-34.04, -86.75) * mm, "radius": 3.18 * mm});
            skCircle(sketch, "E5.8.4.2", {"center": v(-26.25, -82.25) * mm, "radius": 3.18 * mm});
            skCircle(sketch, "E5.8.4.3", {"center": v(-34.04, -77.75) * mm, "radius": 3.18 * mm});
            skCircle(sketch, "E5.8.5.0", {"center": v(-26.25, -55.25) * mm, "radius": 3.18 * mm});
            skCircle(sketch, "E5.8.5.1", {"center": v(-34.04, -68.75) * mm, "radius": 3.18 * mm});
            skCircle(sketch, "E5.8.5.2", {"center": v(-26.25, -64.25) * mm, "radius": 3.18 * mm});
            skCircle(sketch, "E5.8.5.3", {"center": v(-34.04, -59.75) * mm, "radius": 3.18 * mm});
            skCircle(sketch, "E5.8.6.0", {"center": v(-26.25, -37.25) * mm, "radius": 3.18 * mm});
            skCircle(sketch, "E5.8.6.1", {"center": v(-34.04, -50.75) * mm, "radius": 3.18 * mm});
            skCircle(sketch, "E5.8.6.2", {"center": v(-26.25, -46.25) * mm, "radius": 3.18 * mm});
            skCircle(sketch, "E5.8.6.3", {"center": v(-34.04, -41.75) * mm, "radius": 3.18 * mm});
            skCircle(sketch, "E5.8.7.0", {"center": v(-26.25, -19.25) * mm, "radius": 3.18 * mm});
            skCircle(sketch, "E5.8.7.1", {"center": v(-34.04, -32.75) * mm, "radius": 3.18 * mm});
            skCircle(sketch, "E5.8.7.2", {"center": v(-26.25, -28.25) * mm, "radius": 3.18 * mm});
            skCircle(sketch, "E5.8.7.3", {"center": v(-34.04, -23.75) * mm, "radius": 3.18 * mm});
            skCircle(sketch, "E5.8.8.0", {"center": v(-26.25, -1.25) * mm, "radius": 3.18 * mm});
            skCircle(sketch, "E5.8.8.1", {"center": v(-34.04, -14.75) * mm, "radius": 3.18 * mm});
            skCircle(sketch, "E5.8.8.2", {"center": v(-26.25, -10.25) * mm, "radius": 3.18 * mm});
            skCircle(sketch, "E5.8.8.3", {"center": v(-34.04, -5.75) * mm, "radius": 3.18 * mm});
            skCircle(sketch, "E5.8.9.0", {"center": v(-26.25, 16.75) * mm, "radius": 3.18 * mm});
            skCircle(sketch, "E5.8.9.1", {"center": v(-34.04, 3.25) * mm, "radius": 3.18 * mm});
            skCircle(sketch, "E5.8.9.2", {"center": v(-26.25, 7.75) * mm, "radius": 3.18 * mm});
            skCircle(sketch, "E5.8.9.3", {"center": v(-34.04, 12.25) * mm, "radius": 3.18 * mm});
            skCircle(sketch, "E5.8.10.0", {"center": v(-26.25, 34.75) * mm, "radius": 3.18 * mm});
            skCircle(sketch, "E5.8.10.1", {"center": v(-34.04, 21.25) * mm, "radius": 3.18 * mm});
            skCircle(sketch, "E5.8.10.2", {"center": v(-26.25, 25.75) * mm, "radius": 3.18 * mm});
            skCircle(sketch, "E5.8.10.3", {"center": v(-34.04, 30.25) * mm, "radius": 3.18 * mm});
            skCircle(sketch, "E5.8.11.0", {"center": v(-26.25, 52.75) * mm, "radius": 3.18 * mm});
            skCircle(sketch, "E5.8.11.1", {"center": v(-34.04, 39.25) * mm, "radius": 3.18 * mm});
            skCircle(sketch, "E5.8.11.2", {"center": v(-26.25, 43.75) * mm, "radius": 3.18 * mm});
            skCircle(sketch, "E5.8.11.3", {"center": v(-34.04, 48.25) * mm, "radius": 3.18 * mm});
            skCircle(sketch, "E5.8.12.0", {"center": v(-26.25, 70.75) * mm, "radius": 3.18 * mm});
            skCircle(sketch, "E5.8.12.1", {"center": v(-34.04, 57.25) * mm, "radius": 3.18 * mm});
            skCircle(sketch, "E5.8.12.2", {"center": v(-26.25, 61.75) * mm, "radius": 3.18 * mm});
            skCircle(sketch, "E5.8.12.3", {"center": v(-34.04, 66.25) * mm, "radius": 3.18 * mm});
            skCircle(sketch, "E5.8.13.0", {"center": v(-26.25, 88.75) * mm, "radius": 3.18 * mm});
            skCircle(sketch, "E5.8.13.1", {"center": v(-34.04, 75.25) * mm, "radius": 3.18 * mm});
            skCircle(sketch, "E5.8.13.2", {"center": v(-26.25, 79.75) * mm, "radius": 3.18 * mm});
            skCircle(sketch, "E5.8.13.3", {"center": v(-34.04, 84.25) * mm, "radius": 3.18 * mm});
            skCircle(sketch, "E5.8.14.0", {"center": v(-26.25, 106.75) * mm, "radius": 3.18 * mm});
            skCircle(sketch, "E5.8.14.1", {"center": v(-34.04, 93.25) * mm, "radius": 3.18 * mm});
            skCircle(sketch, "E5.8.14.2", {"center": v(-26.25, 97.75) * mm, "radius": 3.18 * mm});
            skCircle(sketch, "E5.8.14.3", {"center": v(-34.04, 102.25) * mm, "radius": 3.18 * mm});
            skCircle(sketch, "E5.8.15.0", {"center": v(-26.25, 124.75) * mm, "radius": 3.18 * mm});
            skCircle(sketch, "E5.8.15.1", {"center": v(-34.04, 111.25) * mm, "radius": 3.18 * mm});
            skCircle(sketch, "E5.8.15.2", {"center": v(-26.25, 115.75) * mm, "radius": 3.18 * mm});
            skCircle(sketch, "E5.8.15.3", {"center": v(-34.04, 120.25) * mm, "radius": 3.18 * mm});
            skCircle(sketch, "E5.8.16.0", {"center": v(-26.25, 142.75) * mm, "radius": 3.18 * mm});
            skCircle(sketch, "E5.8.16.1", {"center": v(-34.04, 129.25) * mm, "radius": 3.18 * mm});
            skCircle(sketch, "E5.8.16.2", {"center": v(-26.25, 133.75) * mm, "radius": 3.18 * mm});
            skCircle(sketch, "E5.8.16.3", {"center": v(-34.04, 138.25) * mm, "radius": 3.18 * mm});
            skCircle(sketch, "E5.8.17.0", {"center": v(-26.25, 160.75) * mm, "radius": 3.18 * mm});
            skCircle(sketch, "E5.8.17.1", {"center": v(-34.04, 147.25) * mm, "radius": 3.18 * mm});
            skCircle(sketch, "E5.8.17.2", {"center": v(-26.25, 151.75) * mm, "radius": 3.18 * mm});
            skCircle(sketch, "E5.8.17.3", {"center": v(-34.04, 156.25) * mm, "radius": 3.18 * mm});
            skCircle(sketch, "E5.9.0.0", {"center": v(-10.66, -145.25) * mm, "radius": 3.18 * mm});
            skCircle(sketch, "E5.9.0.1", {"center": v(-18.45, -158.75) * mm, "radius": 3.18 * mm});
            skCircle(sketch, "E5.9.0.2", {"center": v(-10.66, -154.25) * mm, "radius": 3.18 * mm});
            skCircle(sketch, "E5.9.0.3", {"center": v(-18.45, -149.75) * mm, "radius": 3.18 * mm});
            skCircle(sketch, "E5.9.1.0", {"center": v(-10.66, -127.25) * mm, "radius": 3.18 * mm});
            skCircle(sketch, "E5.9.1.1", {"center": v(-18.45, -140.75) * mm, "radius": 3.18 * mm});
            skCircle(sketch, "E5.9.1.2", {"center": v(-10.66, -136.25) * mm, "radius": 3.18 * mm});
            skCircle(sketch, "E5.9.1.3", {"center": v(-18.45, -131.75) * mm, "radius": 3.18 * mm});
            skCircle(sketch, "E5.9.2.0", {"center": v(-10.66, -109.25) * mm, "radius": 3.18 * mm});
            skCircle(sketch, "E5.9.2.1", {"center": v(-18.45, -122.75) * mm, "radius": 3.18 * mm});
            skCircle(sketch, "E5.9.2.2", {"center": v(-10.66, -118.25) * mm, "radius": 3.18 * mm});
            skCircle(sketch, "E5.9.2.3", {"center": v(-18.45, -113.75) * mm, "radius": 3.18 * mm});
            skCircle(sketch, "E5.9.3.0", {"center": v(-10.66, -91.25) * mm, "radius": 3.18 * mm});
            skCircle(sketch, "E5.9.3.1", {"center": v(-18.45, -104.75) * mm, "radius": 3.18 * mm});
            skCircle(sketch, "E5.9.3.2", {"center": v(-10.66, -100.25) * mm, "radius": 3.18 * mm});
            skCircle(sketch, "E5.9.3.3", {"center": v(-18.45, -95.75) * mm, "radius": 3.18 * mm});
            skCircle(sketch, "E5.9.4.0", {"center": v(-10.66, -73.25) * mm, "radius": 3.18 * mm});
            skCircle(sketch, "E5.9.4.1", {"center": v(-18.45, -86.75) * mm, "radius": 3.18 * mm});
            skCircle(sketch, "E5.9.4.2", {"center": v(-10.66, -82.25) * mm, "radius": 3.18 * mm});
            skCircle(sketch, "E5.9.4.3", {"center": v(-18.45, -77.75) * mm, "radius": 3.18 * mm});
            skCircle(sketch, "E5.9.5.0", {"center": v(-10.66, -55.25) * mm, "radius": 3.18 * mm});
            skCircle(sketch, "E5.9.5.1", {"center": v(-18.45, -68.75) * mm, "radius": 3.18 * mm});
            skCircle(sketch, "E5.9.5.2", {"center": v(-10.66, -64.25) * mm, "radius": 3.18 * mm});
            skCircle(sketch, "E5.9.5.3", {"center": v(-18.45, -59.75) * mm, "radius": 3.18 * mm});
            skCircle(sketch, "E5.9.6.0", {"center": v(-10.66, -37.25) * mm, "radius": 3.18 * mm});
            skCircle(sketch, "E5.9.6.1", {"center": v(-18.45, -50.75) * mm, "radius": 3.18 * mm});
            skCircle(sketch, "E5.9.6.2", {"center": v(-10.66, -46.25) * mm, "radius": 3.18 * mm});
            skCircle(sketch, "E5.9.6.3", {"center": v(-18.45, -41.75) * mm, "radius": 3.18 * mm});
            skCircle(sketch, "E5.9.7.0", {"center": v(-10.66, -19.25) * mm, "radius": 3.18 * mm});
            skCircle(sketch, "E5.9.7.1", {"center": v(-18.45, -32.75) * mm, "radius": 3.18 * mm});
            skCircle(sketch, "E5.9.7.2", {"center": v(-10.66, -28.25) * mm, "radius": 3.18 * mm});
            skCircle(sketch, "E5.9.7.3", {"center": v(-18.45, -23.75) * mm, "radius": 3.18 * mm});
            skCircle(sketch, "E5.9.8.0", {"center": v(-10.66, -1.25) * mm, "radius": 3.18 * mm});
            skCircle(sketch, "E5.9.8.1", {"center": v(-18.45, -14.75) * mm, "radius": 3.18 * mm});
            skCircle(sketch, "E5.9.8.2", {"center": v(-10.66, -10.25) * mm, "radius": 3.18 * mm});
            skCircle(sketch, "E5.9.8.3", {"center": v(-18.45, -5.75) * mm, "radius": 3.18 * mm});
            skCircle(sketch, "E5.9.9.0", {"center": v(-10.66, 16.75) * mm, "radius": 3.18 * mm});
            skCircle(sketch, "E5.9.9.1", {"center": v(-18.45, 3.25) * mm, "radius": 3.18 * mm});
            skCircle(sketch, "E5.9.9.2", {"center": v(-10.66, 7.75) * mm, "radius": 3.18 * mm});
            skCircle(sketch, "E5.9.9.3", {"center": v(-18.45, 12.25) * mm, "radius": 3.18 * mm});
            skCircle(sketch, "E5.9.10.0", {"center": v(-10.66, 34.75) * mm, "radius": 3.18 * mm});
            skCircle(sketch, "E5.9.10.1", {"center": v(-18.45, 21.25) * mm, "radius": 3.18 * mm});
            skCircle(sketch, "E5.9.10.2", {"center": v(-10.66, 25.75) * mm, "radius": 3.18 * mm});
            skCircle(sketch, "E5.9.10.3", {"center": v(-18.45, 30.25) * mm, "radius": 3.18 * mm});
            skCircle(sketch, "E5.9.11.0", {"center": v(-10.66, 52.75) * mm, "radius": 3.18 * mm});
            skCircle(sketch, "E5.9.11.1", {"center": v(-18.45, 39.25) * mm, "radius": 3.18 * mm});
            skCircle(sketch, "E5.9.11.2", {"center": v(-10.66, 43.75) * mm, "radius": 3.18 * mm});
            skCircle(sketch, "E5.9.11.3", {"center": v(-18.45, 48.25) * mm, "radius": 3.18 * mm});
            skCircle(sketch, "E5.9.12.0", {"center": v(-10.66, 70.75) * mm, "radius": 3.18 * mm});
            skCircle(sketch, "E5.9.12.1", {"center": v(-18.45, 57.25) * mm, "radius": 3.18 * mm});
            skCircle(sketch, "E5.9.12.2", {"center": v(-10.66, 61.75) * mm, "radius": 3.18 * mm});
            skCircle(sketch, "E5.9.12.3", {"center": v(-18.45, 66.25) * mm, "radius": 3.18 * mm});
            skCircle(sketch, "E5.9.13.0", {"center": v(-10.66, 88.75) * mm, "radius": 3.18 * mm});
            skCircle(sketch, "E5.9.13.1", {"center": v(-18.45, 75.25) * mm, "radius": 3.18 * mm});
            skCircle(sketch, "E5.9.13.2", {"center": v(-10.66, 79.75) * mm, "radius": 3.18 * mm});
            skCircle(sketch, "E5.9.13.3", {"center": v(-18.45, 84.25) * mm, "radius": 3.18 * mm});
            skCircle(sketch, "E5.9.14.0", {"center": v(-10.66, 106.75) * mm, "radius": 3.18 * mm});
            skCircle(sketch, "E5.9.14.1", {"center": v(-18.45, 93.25) * mm, "radius": 3.18 * mm});
            skCircle(sketch, "E5.9.14.2", {"center": v(-10.66, 97.75) * mm, "radius": 3.18 * mm});
            skCircle(sketch, "E5.9.14.3", {"center": v(-18.45, 102.25) * mm, "radius": 3.18 * mm});
            skCircle(sketch, "E5.9.15.0", {"center": v(-10.66, 124.75) * mm, "radius": 3.18 * mm});
            skCircle(sketch, "E5.9.15.1", {"center": v(-18.45, 111.25) * mm, "radius": 3.18 * mm});
            skCircle(sketch, "E5.9.15.2", {"center": v(-10.66, 115.75) * mm, "radius": 3.18 * mm});
            skCircle(sketch, "E5.9.15.3", {"center": v(-18.45, 120.25) * mm, "radius": 3.18 * mm});
            skCircle(sketch, "E5.9.16.0", {"center": v(-10.66, 142.75) * mm, "radius": 3.18 * mm});
            skCircle(sketch, "E5.9.16.1", {"center": v(-18.45, 129.25) * mm, "radius": 3.18 * mm});
            skCircle(sketch, "E5.9.16.2", {"center": v(-10.66, 133.75) * mm, "radius": 3.18 * mm});
            skCircle(sketch, "E5.9.16.3", {"center": v(-18.45, 138.25) * mm, "radius": 3.18 * mm});
            skCircle(sketch, "E5.9.17.0", {"center": v(-10.66, 160.75) * mm, "radius": 3.18 * mm});
            skCircle(sketch, "E5.9.17.1", {"center": v(-18.45, 147.25) * mm, "radius": 3.18 * mm});
            skCircle(sketch, "E5.9.17.2", {"center": v(-10.66, 151.75) * mm, "radius": 3.18 * mm});
            skCircle(sketch, "E5.9.17.3", {"center": v(-18.45, 156.25) * mm, "radius": 3.18 * mm});
            skCircle(sketch, "E5.10.0.0", {"center": v(4.93, -145.25) * mm, "radius": 3.18 * mm});
            skCircle(sketch, "E5.10.0.1", {"center": v(-2.87, -158.75) * mm, "radius": 3.18 * mm});
            skCircle(sketch, "E5.10.0.2", {"center": v(4.93, -154.25) * mm, "radius": 3.18 * mm});
            skCircle(sketch, "E5.10.0.3", {"center": v(-2.87, -149.75) * mm, "radius": 3.18 * mm});
            skCircle(sketch, "E5.10.1.0", {"center": v(4.93, -127.25) * mm, "radius": 3.18 * mm});
            skCircle(sketch, "E5.10.1.1", {"center": v(-2.87, -140.75) * mm, "radius": 3.18 * mm});
            skCircle(sketch, "E5.10.1.2", {"center": v(4.93, -136.25) * mm, "radius": 3.18 * mm});
            skCircle(sketch, "E5.10.1.3", {"center": v(-2.87, -131.75) * mm, "radius": 3.18 * mm});
            skCircle(sketch, "E5.10.2.0", {"center": v(4.93, -109.25) * mm, "radius": 3.18 * mm});
            skCircle(sketch, "E5.10.2.1", {"center": v(-2.87, -122.75) * mm, "radius": 3.18 * mm});
            skCircle(sketch, "E5.10.2.2", {"center": v(4.93, -118.25) * mm, "radius": 3.18 * mm});
            skCircle(sketch, "E5.10.2.3", {"center": v(-2.87, -113.75) * mm, "radius": 3.18 * mm});
            skCircle(sketch, "E5.10.3.0", {"center": v(4.93, -91.25) * mm, "radius": 3.18 * mm});
            skCircle(sketch, "E5.10.3.1", {"center": v(-2.87, -104.75) * mm, "radius": 3.18 * mm});
            skCircle(sketch, "E5.10.3.2", {"center": v(4.93, -100.25) * mm, "radius": 3.18 * mm});
            skCircle(sketch, "E5.10.3.3", {"center": v(-2.87, -95.75) * mm, "radius": 3.18 * mm});
            skCircle(sketch, "E5.10.4.0", {"center": v(4.93, -73.25) * mm, "radius": 3.18 * mm});
            skCircle(sketch, "E5.10.4.1", {"center": v(-2.87, -86.75) * mm, "radius": 3.18 * mm});
            skCircle(sketch, "E5.10.4.2", {"center": v(4.93, -82.25) * mm, "radius": 3.18 * mm});
            skCircle(sketch, "E5.10.4.3", {"center": v(-2.87, -77.75) * mm, "radius": 3.18 * mm});
            skCircle(sketch, "E5.10.5.0", {"center": v(4.93, -55.25) * mm, "radius": 3.18 * mm});
            skCircle(sketch, "E5.10.5.1", {"center": v(-2.87, -68.75) * mm, "radius": 3.18 * mm});
            skCircle(sketch, "E5.10.5.2", {"center": v(4.93, -64.25) * mm, "radius": 3.18 * mm});
            skCircle(sketch, "E5.10.5.3", {"center": v(-2.87, -59.75) * mm, "radius": 3.18 * mm});
            skCircle(sketch, "E5.10.6.0", {"center": v(4.93, -37.25) * mm, "radius": 3.18 * mm});
            skCircle(sketch, "E5.10.6.1", {"center": v(-2.87, -50.75) * mm, "radius": 3.18 * mm});
            skCircle(sketch, "E5.10.6.2", {"center": v(4.93, -46.25) * mm, "radius": 3.18 * mm});
            skCircle(sketch, "E5.10.6.3", {"center": v(-2.87, -41.75) * mm, "radius": 3.18 * mm});
            skCircle(sketch, "E5.10.7.0", {"center": v(4.93, -19.25) * mm, "radius": 3.18 * mm});
            skCircle(sketch, "E5.10.7.1", {"center": v(-2.87, -32.75) * mm, "radius": 3.18 * mm});
            skCircle(sketch, "E5.10.7.2", {"center": v(4.93, -28.25) * mm, "radius": 3.18 * mm});
            skCircle(sketch, "E5.10.7.3", {"center": v(-2.87, -23.75) * mm, "radius": 3.18 * mm});
            skCircle(sketch, "E5.10.8.0", {"center": v(4.93, -1.25) * mm, "radius": 3.18 * mm});
            skCircle(sketch, "E5.10.8.1", {"center": v(-2.87, -14.75) * mm, "radius": 3.18 * mm});
            skCircle(sketch, "E5.10.8.2", {"center": v(4.93, -10.25) * mm, "radius": 3.18 * mm});
            skCircle(sketch, "E5.10.8.3", {"center": v(-2.87, -5.75) * mm, "radius": 3.18 * mm});
            skCircle(sketch, "E5.10.9.0", {"center": v(4.93, 16.75) * mm, "radius": 3.18 * mm});
            skCircle(sketch, "E5.10.9.1", {"center": v(-2.87, 3.25) * mm, "radius": 3.18 * mm});
            skCircle(sketch, "E5.10.9.2", {"center": v(4.93, 7.75) * mm, "radius": 3.18 * mm});
            skCircle(sketch, "E5.10.9.3", {"center": v(-2.87, 12.25) * mm, "radius": 3.18 * mm});
            skCircle(sketch, "E5.10.10.0", {"center": v(4.93, 34.75) * mm, "radius": 3.18 * mm});
            skCircle(sketch, "E5.10.10.1", {"center": v(-2.87, 21.25) * mm, "radius": 3.18 * mm});
            skCircle(sketch, "E5.10.10.2", {"center": v(4.93, 25.75) * mm, "radius": 3.18 * mm});
            skCircle(sketch, "E5.10.10.3", {"center": v(-2.87, 30.25) * mm, "radius": 3.18 * mm});
            skCircle(sketch, "E5.10.11.0", {"center": v(4.93, 52.75) * mm, "radius": 3.18 * mm});
            skCircle(sketch, "E5.10.11.1", {"center": v(-2.87, 39.25) * mm, "radius": 3.18 * mm});
            skCircle(sketch, "E5.10.11.2", {"center": v(4.93, 43.75) * mm, "radius": 3.18 * mm});
            skCircle(sketch, "E5.10.11.3", {"center": v(-2.87, 48.25) * mm, "radius": 3.18 * mm});
            skCircle(sketch, "E5.10.12.0", {"center": v(4.93, 70.75) * mm, "radius": 3.18 * mm});
            skCircle(sketch, "E5.10.12.1", {"center": v(-2.87, 57.25) * mm, "radius": 3.18 * mm});
            skCircle(sketch, "E5.10.12.2", {"center": v(4.93, 61.75) * mm, "radius": 3.18 * mm});
            skCircle(sketch, "E5.10.12.3", {"center": v(-2.87, 66.25) * mm, "radius": 3.18 * mm});
            skCircle(sketch, "E5.10.13.0", {"center": v(4.93, 88.75) * mm, "radius": 3.18 * mm});
            skCircle(sketch, "E5.10.13.1", {"center": v(-2.87, 75.25) * mm, "radius": 3.18 * mm});
            skCircle(sketch, "E5.10.13.2", {"center": v(4.93, 79.75) * mm, "radius": 3.18 * mm});
            skCircle(sketch, "E5.10.13.3", {"center": v(-2.87, 84.25) * mm, "radius": 3.18 * mm});
            skCircle(sketch, "E5.10.14.0", {"center": v(4.93, 106.75) * mm, "radius": 3.18 * mm});
            skCircle(sketch, "E5.10.14.1", {"center": v(-2.87, 93.25) * mm, "radius": 3.18 * mm});
            skCircle(sketch, "E5.10.14.2", {"center": v(4.93, 97.75) * mm, "radius": 3.18 * mm});
            skCircle(sketch, "E5.10.14.3", {"center": v(-2.87, 102.25) * mm, "radius": 3.18 * mm});
            skCircle(sketch, "E5.10.15.0", {"center": v(4.93, 124.75) * mm, "radius": 3.18 * mm});
            skCircle(sketch, "E5.10.15.1", {"center": v(-2.87, 111.25) * mm, "radius": 3.18 * mm});
            skCircle(sketch, "E5.10.15.2", {"center": v(4.93, 115.75) * mm, "radius": 3.18 * mm});
            skCircle(sketch, "E5.10.15.3", {"center": v(-2.87, 120.25) * mm, "radius": 3.18 * mm});
            skCircle(sketch, "E5.10.16.0", {"center": v(4.93, 142.75) * mm, "radius": 3.18 * mm});
            skCircle(sketch, "E5.10.16.1", {"center": v(-2.87, 129.25) * mm, "radius": 3.18 * mm});
            skCircle(sketch, "E5.10.16.2", {"center": v(4.93, 133.75) * mm, "radius": 3.18 * mm});
            skCircle(sketch, "E5.10.16.3", {"center": v(-2.87, 138.25) * mm, "radius": 3.18 * mm});
            skCircle(sketch, "E5.10.17.0", {"center": v(4.93, 160.75) * mm, "radius": 3.18 * mm});
            skCircle(sketch, "E5.10.17.1", {"center": v(-2.87, 147.25) * mm, "radius": 3.18 * mm});
            skCircle(sketch, "E5.10.17.2", {"center": v(4.93, 151.75) * mm, "radius": 3.18 * mm});
            skCircle(sketch, "E5.10.17.3", {"center": v(-2.87, 156.25) * mm, "radius": 3.18 * mm});
            skCircle(sketch, "E5.11.0.0", {"center": v(20.52, -145.25) * mm, "radius": 3.18 * mm});
            skCircle(sketch, "E5.11.0.1", {"center": v(12.72, -158.75) * mm, "radius": 3.18 * mm});
            skCircle(sketch, "E5.11.0.2", {"center": v(20.52, -154.25) * mm, "radius": 3.18 * mm});
            skCircle(sketch, "E5.11.0.3", {"center": v(12.72, -149.75) * mm, "radius": 3.18 * mm});
            skCircle(sketch, "E5.11.1.0", {"center": v(20.52, -127.25) * mm, "radius": 3.18 * mm});
            skCircle(sketch, "E5.11.1.1", {"center": v(12.72, -140.75) * mm, "radius": 3.18 * mm});
            skCircle(sketch, "E5.11.1.2", {"center": v(20.52, -136.25) * mm, "radius": 3.18 * mm});
            skCircle(sketch, "E5.11.1.3", {"center": v(12.72, -131.75) * mm, "radius": 3.18 * mm});
            skCircle(sketch, "E5.11.2.0", {"center": v(20.52, -109.25) * mm, "radius": 3.18 * mm});
            skCircle(sketch, "E5.11.2.1", {"center": v(12.72, -122.75) * mm, "radius": 3.18 * mm});
            skCircle(sketch, "E5.11.2.2", {"center": v(20.52, -118.25) * mm, "radius": 3.18 * mm});
            skCircle(sketch, "E5.11.2.3", {"center": v(12.72, -113.75) * mm, "radius": 3.18 * mm});
            skCircle(sketch, "E5.11.3.0", {"center": v(20.52, -91.25) * mm, "radius": 3.18 * mm});
            skCircle(sketch, "E5.11.3.1", {"center": v(12.72, -104.75) * mm, "radius": 3.18 * mm});
            skCircle(sketch, "E5.11.3.2", {"center": v(20.52, -100.25) * mm, "radius": 3.18 * mm});
            skCircle(sketch, "E5.11.3.3", {"center": v(12.72, -95.75) * mm, "radius": 3.18 * mm});
            skCircle(sketch, "E5.11.4.0", {"center": v(20.52, -73.25) * mm, "radius": 3.18 * mm});
            skCircle(sketch, "E5.11.4.1", {"center": v(12.72, -86.75) * mm, "radius": 3.18 * mm});
            skCircle(sketch, "E5.11.4.2", {"center": v(20.52, -82.25) * mm, "radius": 3.18 * mm});
            skCircle(sketch, "E5.11.4.3", {"center": v(12.72, -77.75) * mm, "radius": 3.18 * mm});
            skCircle(sketch, "E5.11.5.0", {"center": v(20.52, -55.25) * mm, "radius": 3.18 * mm});
            skCircle(sketch, "E5.11.5.1", {"center": v(12.72, -68.75) * mm, "radius": 3.18 * mm});
            skCircle(sketch, "E5.11.5.2", {"center": v(20.52, -64.25) * mm, "radius": 3.18 * mm});
            skCircle(sketch, "E5.11.5.3", {"center": v(12.72, -59.75) * mm, "radius": 3.18 * mm});
            skCircle(sketch, "E5.11.6.0", {"center": v(20.52, -37.25) * mm, "radius": 3.18 * mm});
            skCircle(sketch, "E5.11.6.1", {"center": v(12.72, -50.75) * mm, "radius": 3.18 * mm});
            skCircle(sketch, "E5.11.6.2", {"center": v(20.52, -46.25) * mm, "radius": 3.18 * mm});
            skCircle(sketch, "E5.11.6.3", {"center": v(12.72, -41.75) * mm, "radius": 3.18 * mm});
            skCircle(sketch, "E5.11.7.0", {"center": v(20.52, -19.25) * mm, "radius": 3.18 * mm});
            skCircle(sketch, "E5.11.7.1", {"center": v(12.72, -32.75) * mm, "radius": 3.18 * mm});
            skCircle(sketch, "E5.11.7.2", {"center": v(20.52, -28.25) * mm, "radius": 3.18 * mm});
            skCircle(sketch, "E5.11.7.3", {"center": v(12.72, -23.75) * mm, "radius": 3.18 * mm});
            skCircle(sketch, "E5.11.8.0", {"center": v(20.52, -1.25) * mm, "radius": 3.18 * mm});
            skCircle(sketch, "E5.11.8.1", {"center": v(12.72, -14.75) * mm, "radius": 3.18 * mm});
            skCircle(sketch, "E5.11.8.2", {"center": v(20.52, -10.25) * mm, "radius": 3.18 * mm});
            skCircle(sketch, "E5.11.8.3", {"center": v(12.72, -5.75) * mm, "radius": 3.18 * mm});
            skCircle(sketch, "E5.11.9.0", {"center": v(20.52, 16.75) * mm, "radius": 3.18 * mm});
            skCircle(sketch, "E5.11.9.1", {"center": v(12.72, 3.25) * mm, "radius": 3.18 * mm});
            skCircle(sketch, "E5.11.9.2", {"center": v(20.52, 7.75) * mm, "radius": 3.18 * mm});
            skCircle(sketch, "E5.11.9.3", {"center": v(12.72, 12.25) * mm, "radius": 3.18 * mm});
            skCircle(sketch, "E5.11.10.0", {"center": v(20.52, 34.75) * mm, "radius": 3.18 * mm});
            skCircle(sketch, "E5.11.10.1", {"center": v(12.72, 21.25) * mm, "radius": 3.18 * mm});
            skCircle(sketch, "E5.11.10.2", {"center": v(20.52, 25.75) * mm, "radius": 3.18 * mm});
            skCircle(sketch, "E5.11.10.3", {"center": v(12.72, 30.25) * mm, "radius": 3.18 * mm});
            skCircle(sketch, "E5.11.11.0", {"center": v(20.52, 52.75) * mm, "radius": 3.18 * mm});
            skCircle(sketch, "E5.11.11.1", {"center": v(12.72, 39.25) * mm, "radius": 3.18 * mm});
            skCircle(sketch, "E5.11.11.2", {"center": v(20.52, 43.75) * mm, "radius": 3.18 * mm});
            skCircle(sketch, "E5.11.11.3", {"center": v(12.72, 48.25) * mm, "radius": 3.18 * mm});
            skCircle(sketch, "E5.11.12.0", {"center": v(20.52, 70.75) * mm, "radius": 3.18 * mm});
            skCircle(sketch, "E5.11.12.1", {"center": v(12.72, 57.25) * mm, "radius": 3.18 * mm});
            skCircle(sketch, "E5.11.12.2", {"center": v(20.52, 61.75) * mm, "radius": 3.18 * mm});
            skCircle(sketch, "E5.11.12.3", {"center": v(12.72, 66.25) * mm, "radius": 3.18 * mm});
            skCircle(sketch, "E5.11.13.0", {"center": v(20.52, 88.75) * mm, "radius": 3.18 * mm});
            skCircle(sketch, "E5.11.13.1", {"center": v(12.72, 75.25) * mm, "radius": 3.18 * mm});
            skCircle(sketch, "E5.11.13.2", {"center": v(20.52, 79.75) * mm, "radius": 3.18 * mm});
            skCircle(sketch, "E5.11.13.3", {"center": v(12.72, 84.25) * mm, "radius": 3.18 * mm});
            skCircle(sketch, "E5.11.14.0", {"center": v(20.52, 106.75) * mm, "radius": 3.18 * mm});
            skCircle(sketch, "E5.11.14.1", {"center": v(12.72, 93.25) * mm, "radius": 3.18 * mm});
            skCircle(sketch, "E5.11.14.2", {"center": v(20.52, 97.75) * mm, "radius": 3.18 * mm});
            skCircle(sketch, "E5.11.14.3", {"center": v(12.72, 102.25) * mm, "radius": 3.18 * mm});
            skCircle(sketch, "E5.11.15.0", {"center": v(20.52, 124.75) * mm, "radius": 3.18 * mm});
            skCircle(sketch, "E5.11.15.1", {"center": v(12.72, 111.25) * mm, "radius": 3.18 * mm});
            skCircle(sketch, "E5.11.15.2", {"center": v(20.52, 115.75) * mm, "radius": 3.18 * mm});
            skCircle(sketch, "E5.11.15.3", {"center": v(12.72, 120.25) * mm, "radius": 3.18 * mm});
            skCircle(sketch, "E5.11.16.0", {"center": v(20.52, 142.75) * mm, "radius": 3.18 * mm});
            skCircle(sketch, "E5.11.16.1", {"center": v(12.72, 129.25) * mm, "radius": 3.18 * mm});
            skCircle(sketch, "E5.11.16.2", {"center": v(20.52, 133.75) * mm, "radius": 3.18 * mm});
            skCircle(sketch, "E5.11.16.3", {"center": v(12.72, 138.25) * mm, "radius": 3.18 * mm});
            skCircle(sketch, "E5.11.17.0", {"center": v(20.52, 160.75) * mm, "radius": 3.18 * mm});
            skCircle(sketch, "E5.11.17.1", {"center": v(12.72, 147.25) * mm, "radius": 3.18 * mm});
            skCircle(sketch, "E5.11.17.2", {"center": v(20.52, 151.75) * mm, "radius": 3.18 * mm});
            skCircle(sketch, "E5.11.17.3", {"center": v(12.72, 156.25) * mm, "radius": 3.18 * mm});
            skCircle(sketch, "E5.12.0.0", {"center": v(36.1, -145.25) * mm, "radius": 3.18 * mm});
            skCircle(sketch, "E5.12.0.1", {"center": v(28.31, -158.75) * mm, "radius": 3.18 * mm});
            skCircle(sketch, "E5.12.0.2", {"center": v(36.1, -154.25) * mm, "radius": 3.18 * mm});
            skCircle(sketch, "E5.12.0.3", {"center": v(28.31, -149.75) * mm, "radius": 3.18 * mm});
            skCircle(sketch, "E5.12.1.0", {"center": v(36.1, -127.25) * mm, "radius": 3.18 * mm});
            skCircle(sketch, "E5.12.1.1", {"center": v(28.31, -140.75) * mm, "radius": 3.18 * mm});
            skCircle(sketch, "E5.12.1.2", {"center": v(36.1, -136.25) * mm, "radius": 3.18 * mm});
            skCircle(sketch, "E5.12.1.3", {"center": v(28.31, -131.75) * mm, "radius": 3.18 * mm});
            skCircle(sketch, "E5.12.2.0", {"center": v(36.1, -109.25) * mm, "radius": 3.18 * mm});
            skCircle(sketch, "E5.12.2.1", {"center": v(28.31, -122.75) * mm, "radius": 3.18 * mm});
            skCircle(sketch, "E5.12.2.2", {"center": v(36.1, -118.25) * mm, "radius": 3.18 * mm});
            skCircle(sketch, "E5.12.2.3", {"center": v(28.31, -113.75) * mm, "radius": 3.18 * mm});
            skCircle(sketch, "E5.12.3.0", {"center": v(36.1, -91.25) * mm, "radius": 3.18 * mm});
            skCircle(sketch, "E5.12.3.1", {"center": v(28.31, -104.75) * mm, "radius": 3.18 * mm});
            skCircle(sketch, "E5.12.3.2", {"center": v(36.1, -100.25) * mm, "radius": 3.18 * mm});
            skCircle(sketch, "E5.12.3.3", {"center": v(28.31, -95.75) * mm, "radius": 3.18 * mm});
            skCircle(sketch, "E5.12.4.0", {"center": v(36.1, -73.25) * mm, "radius": 3.18 * mm});
            skCircle(sketch, "E5.12.4.1", {"center": v(28.31, -86.75) * mm, "radius": 3.18 * mm});
            skCircle(sketch, "E5.12.4.2", {"center": v(36.1, -82.25) * mm, "radius": 3.18 * mm});
            skCircle(sketch, "E5.12.4.3", {"center": v(28.31, -77.75) * mm, "radius": 3.18 * mm});
            skCircle(sketch, "E5.12.5.0", {"center": v(36.1, -55.25) * mm, "radius": 3.18 * mm});
            skCircle(sketch, "E5.12.5.1", {"center": v(28.31, -68.75) * mm, "radius": 3.18 * mm});
            skCircle(sketch, "E5.12.5.2", {"center": v(36.1, -64.25) * mm, "radius": 3.18 * mm});
            skCircle(sketch, "E5.12.5.3", {"center": v(28.31, -59.75) * mm, "radius": 3.18 * mm});
            skCircle(sketch, "E5.12.6.0", {"center": v(36.1, -37.25) * mm, "radius": 3.18 * mm});
            skCircle(sketch, "E5.12.6.1", {"center": v(28.31, -50.75) * mm, "radius": 3.18 * mm});
            skCircle(sketch, "E5.12.6.2", {"center": v(36.1, -46.25) * mm, "radius": 3.18 * mm});
            skCircle(sketch, "E5.12.6.3", {"center": v(28.31, -41.75) * mm, "radius": 3.18 * mm});
            skCircle(sketch, "E5.12.7.0", {"center": v(36.1, -19.25) * mm, "radius": 3.18 * mm});
            skCircle(sketch, "E5.12.7.1", {"center": v(28.31, -32.75) * mm, "radius": 3.18 * mm});
            skCircle(sketch, "E5.12.7.2", {"center": v(36.1, -28.25) * mm, "radius": 3.18 * mm});
            skCircle(sketch, "E5.12.7.3", {"center": v(28.31, -23.75) * mm, "radius": 3.18 * mm});
            skCircle(sketch, "E5.12.8.0", {"center": v(36.1, -1.25) * mm, "radius": 3.18 * mm});
            skCircle(sketch, "E5.12.8.1", {"center": v(28.31, -14.75) * mm, "radius": 3.18 * mm});
            skCircle(sketch, "E5.12.8.2", {"center": v(36.1, -10.25) * mm, "radius": 3.18 * mm});
            skCircle(sketch, "E5.12.8.3", {"center": v(28.31, -5.75) * mm, "radius": 3.18 * mm});
            skCircle(sketch, "E5.12.9.0", {"center": v(36.1, 16.75) * mm, "radius": 3.18 * mm});
            skCircle(sketch, "E5.12.9.1", {"center": v(28.31, 3.25) * mm, "radius": 3.18 * mm});
            skCircle(sketch, "E5.12.9.2", {"center": v(36.1, 7.75) * mm, "radius": 3.18 * mm});
            skCircle(sketch, "E5.12.9.3", {"center": v(28.31, 12.25) * mm, "radius": 3.18 * mm});
            skCircle(sketch, "E5.12.10.0", {"center": v(36.1, 34.75) * mm, "radius": 3.18 * mm});
            skCircle(sketch, "E5.12.10.1", {"center": v(28.31, 21.25) * mm, "radius": 3.18 * mm});
            skCircle(sketch, "E5.12.10.2", {"center": v(36.1, 25.75) * mm, "radius": 3.18 * mm});
            skCircle(sketch, "E5.12.10.3", {"center": v(28.31, 30.25) * mm, "radius": 3.18 * mm});
            skCircle(sketch, "E5.12.11.0", {"center": v(36.1, 52.75) * mm, "radius": 3.18 * mm});
            skCircle(sketch, "E5.12.11.1", {"center": v(28.31, 39.25) * mm, "radius": 3.18 * mm});
            skCircle(sketch, "E5.12.11.2", {"center": v(36.1, 43.75) * mm, "radius": 3.18 * mm});
            skCircle(sketch, "E5.12.11.3", {"center": v(28.31, 48.25) * mm, "radius": 3.18 * mm});
            skCircle(sketch, "E5.12.12.0", {"center": v(36.1, 70.75) * mm, "radius": 3.18 * mm});
            skCircle(sketch, "E5.12.12.1", {"center": v(28.31, 57.25) * mm, "radius": 3.18 * mm});
            skCircle(sketch, "E5.12.12.2", {"center": v(36.1, 61.75) * mm, "radius": 3.18 * mm});
            skCircle(sketch, "E5.12.12.3", {"center": v(28.31, 66.25) * mm, "radius": 3.18 * mm});
            skCircle(sketch, "E5.12.13.0", {"center": v(36.1, 88.75) * mm, "radius": 3.18 * mm});
            skCircle(sketch, "E5.12.13.1", {"center": v(28.31, 75.25) * mm, "radius": 3.18 * mm});
            skCircle(sketch, "E5.12.13.2", {"center": v(36.1, 79.75) * mm, "radius": 3.18 * mm});
            skCircle(sketch, "E5.12.13.3", {"center": v(28.31, 84.25) * mm, "radius": 3.18 * mm});
            skCircle(sketch, "E5.12.14.0", {"center": v(36.1, 106.75) * mm, "radius": 3.18 * mm});
            skCircle(sketch, "E5.12.14.1", {"center": v(28.31, 93.25) * mm, "radius": 3.18 * mm});
            skCircle(sketch, "E5.12.14.2", {"center": v(36.1, 97.75) * mm, "radius": 3.18 * mm});
            skCircle(sketch, "E5.12.14.3", {"center": v(28.31, 102.25) * mm, "radius": 3.18 * mm});
            skCircle(sketch, "E5.12.15.0", {"center": v(36.1, 124.75) * mm, "radius": 3.18 * mm});
            skCircle(sketch, "E5.12.15.1", {"center": v(28.31, 111.25) * mm, "radius": 3.18 * mm});
            skCircle(sketch, "E5.12.15.2", {"center": v(36.1, 115.75) * mm, "radius": 3.18 * mm});
            skCircle(sketch, "E5.12.15.3", {"center": v(28.31, 120.25) * mm, "radius": 3.18 * mm});
            skCircle(sketch, "E5.12.16.0", {"center": v(36.1, 142.75) * mm, "radius": 3.18 * mm});
            skCircle(sketch, "E5.12.16.1", {"center": v(28.31, 129.25) * mm, "radius": 3.18 * mm});
            skCircle(sketch, "E5.12.16.2", {"center": v(36.1, 133.75) * mm, "radius": 3.18 * mm});
            skCircle(sketch, "E5.12.16.3", {"center": v(28.31, 138.25) * mm, "radius": 3.18 * mm});
            skCircle(sketch, "E5.12.17.0", {"center": v(36.1, 160.75) * mm, "radius": 3.18 * mm});
            skCircle(sketch, "E5.12.17.1", {"center": v(28.31, 147.25) * mm, "radius": 3.18 * mm});
            skCircle(sketch, "E5.12.17.2", {"center": v(36.1, 151.75) * mm, "radius": 3.18 * mm});
            skCircle(sketch, "E5.12.17.3", {"center": v(28.31, 156.25) * mm, "radius": 3.18 * mm});
            skCircle(sketch, "E5.13.0.0", {"center": v(51.7, -145.25) * mm, "radius": 3.18 * mm});
            skCircle(sketch, "E5.13.0.1", {"center": v(43.9, -158.75) * mm, "radius": 3.18 * mm});
            skCircle(sketch, "E5.13.0.2", {"center": v(51.7, -154.25) * mm, "radius": 3.18 * mm});
            skCircle(sketch, "E5.13.0.3", {"center": v(43.9, -149.75) * mm, "radius": 3.18 * mm});
            skCircle(sketch, "E5.13.1.0", {"center": v(51.7, -127.25) * mm, "radius": 3.18 * mm});
            skCircle(sketch, "E5.13.1.1", {"center": v(43.9, -140.75) * mm, "radius": 3.18 * mm});
            skCircle(sketch, "E5.13.1.2", {"center": v(51.7, -136.25) * mm, "radius": 3.18 * mm});
            skCircle(sketch, "E5.13.1.3", {"center": v(43.9, -131.75) * mm, "radius": 3.18 * mm});
            skCircle(sketch, "E5.13.2.0", {"center": v(51.7, -109.25) * mm, "radius": 3.18 * mm});
            skCircle(sketch, "E5.13.2.1", {"center": v(43.9, -122.75) * mm, "radius": 3.18 * mm});
            skCircle(sketch, "E5.13.2.2", {"center": v(51.7, -118.25) * mm, "radius": 3.18 * mm});
            skCircle(sketch, "E5.13.2.3", {"center": v(43.9, -113.75) * mm, "radius": 3.18 * mm});
            skCircle(sketch, "E5.13.3.0", {"center": v(51.7, -91.25) * mm, "radius": 3.18 * mm});
            skCircle(sketch, "E5.13.3.1", {"center": v(43.9, -104.75) * mm, "radius": 3.18 * mm});
            skCircle(sketch, "E5.13.3.2", {"center": v(51.7, -100.25) * mm, "radius": 3.18 * mm});
            skCircle(sketch, "E5.13.3.3", {"center": v(43.9, -95.75) * mm, "radius": 3.18 * mm});
            skCircle(sketch, "E5.13.4.0", {"center": v(51.7, -73.25) * mm, "radius": 3.18 * mm});
            skCircle(sketch, "E5.13.4.1", {"center": v(43.9, -86.75) * mm, "radius": 3.18 * mm});
            skCircle(sketch, "E5.13.4.2", {"center": v(51.7, -82.25) * mm, "radius": 3.18 * mm});
            skCircle(sketch, "E5.13.4.3", {"center": v(43.9, -77.75) * mm, "radius": 3.18 * mm});
            skCircle(sketch, "E5.13.5.0", {"center": v(51.7, -55.25) * mm, "radius": 3.18 * mm});
            skCircle(sketch, "E5.13.5.1", {"center": v(43.9, -68.75) * mm, "radius": 3.18 * mm});
            skCircle(sketch, "E5.13.5.2", {"center": v(51.7, -64.25) * mm, "radius": 3.18 * mm});
            skCircle(sketch, "E5.13.5.3", {"center": v(43.9, -59.75) * mm, "radius": 3.18 * mm});
            skCircle(sketch, "E5.13.6.0", {"center": v(51.7, -37.25) * mm, "radius": 3.18 * mm});
            skCircle(sketch, "E5.13.6.1", {"center": v(43.9, -50.75) * mm, "radius": 3.18 * mm});
            skCircle(sketch, "E5.13.6.2", {"center": v(51.7, -46.25) * mm, "radius": 3.18 * mm});
            skCircle(sketch, "E5.13.6.3", {"center": v(43.9, -41.75) * mm, "radius": 3.18 * mm});
            skCircle(sketch, "E5.13.7.0", {"center": v(51.7, -19.25) * mm, "radius": 3.18 * mm});
            skCircle(sketch, "E5.13.7.1", {"center": v(43.9, -32.75) * mm, "radius": 3.18 * mm});
            skCircle(sketch, "E5.13.7.2", {"center": v(51.7, -28.25) * mm, "radius": 3.18 * mm});
            skCircle(sketch, "E5.13.7.3", {"center": v(43.9, -23.75) * mm, "radius": 3.18 * mm});
            skCircle(sketch, "E5.13.8.0", {"center": v(51.7, -1.25) * mm, "radius": 3.18 * mm});
            skCircle(sketch, "E5.13.8.1", {"center": v(43.9, -14.75) * mm, "radius": 3.18 * mm});
            skCircle(sketch, "E5.13.8.2", {"center": v(51.7, -10.25) * mm, "radius": 3.18 * mm});
            skCircle(sketch, "E5.13.8.3", {"center": v(43.9, -5.75) * mm, "radius": 3.18 * mm});
            skCircle(sketch, "E5.13.9.0", {"center": v(51.7, 16.75) * mm, "radius": 3.18 * mm});
            skCircle(sketch, "E5.13.9.1", {"center": v(43.9, 3.25) * mm, "radius": 3.18 * mm});
            skCircle(sketch, "E5.13.9.2", {"center": v(51.7, 7.75) * mm, "radius": 3.18 * mm});
            skCircle(sketch, "E5.13.9.3", {"center": v(43.9, 12.25) * mm, "radius": 3.18 * mm});
            skCircle(sketch, "E5.13.10.0", {"center": v(51.7, 34.75) * mm, "radius": 3.18 * mm});
            skCircle(sketch, "E5.13.10.1", {"center": v(43.9, 21.25) * mm, "radius": 3.18 * mm});
            skCircle(sketch, "E5.13.10.2", {"center": v(51.7, 25.75) * mm, "radius": 3.18 * mm});
            skCircle(sketch, "E5.13.10.3", {"center": v(43.9, 30.25) * mm, "radius": 3.18 * mm});
            skCircle(sketch, "E5.13.11.0", {"center": v(51.7, 52.75) * mm, "radius": 3.18 * mm});
            skCircle(sketch, "E5.13.11.1", {"center": v(43.9, 39.25) * mm, "radius": 3.18 * mm});
            skCircle(sketch, "E5.13.11.2", {"center": v(51.7, 43.75) * mm, "radius": 3.18 * mm});
            skCircle(sketch, "E5.13.11.3", {"center": v(43.9, 48.25) * mm, "radius": 3.18 * mm});
            skCircle(sketch, "E5.13.12.0", {"center": v(51.7, 70.75) * mm, "radius": 3.18 * mm});
            skCircle(sketch, "E5.13.12.1", {"center": v(43.9, 57.25) * mm, "radius": 3.18 * mm});
            skCircle(sketch, "E5.13.12.2", {"center": v(51.7, 61.75) * mm, "radius": 3.18 * mm});
            skCircle(sketch, "E5.13.12.3", {"center": v(43.9, 66.25) * mm, "radius": 3.18 * mm});
            skCircle(sketch, "E5.13.13.0", {"center": v(51.7, 88.75) * mm, "radius": 3.18 * mm});
            skCircle(sketch, "E5.13.13.1", {"center": v(43.9, 75.25) * mm, "radius": 3.18 * mm});
            skCircle(sketch, "E5.13.13.2", {"center": v(51.7, 79.75) * mm, "radius": 3.18 * mm});
            skCircle(sketch, "E5.13.13.3", {"center": v(43.9, 84.25) * mm, "radius": 3.18 * mm});
            skCircle(sketch, "E5.13.14.0", {"center": v(51.7, 106.75) * mm, "radius": 3.18 * mm});
            skCircle(sketch, "E5.13.14.1", {"center": v(43.9, 93.25) * mm, "radius": 3.18 * mm});
            skCircle(sketch, "E5.13.14.2", {"center": v(51.7, 97.75) * mm, "radius": 3.18 * mm});
            skCircle(sketch, "E5.13.14.3", {"center": v(43.9, 102.25) * mm, "radius": 3.18 * mm});
            skCircle(sketch, "E5.13.15.0", {"center": v(51.7, 124.75) * mm, "radius": 3.18 * mm});
            skCircle(sketch, "E5.13.15.1", {"center": v(43.9, 111.25) * mm, "radius": 3.18 * mm});
            skCircle(sketch, "E5.13.15.2", {"center": v(51.7, 115.75) * mm, "radius": 3.18 * mm});
            skCircle(sketch, "E5.13.15.3", {"center": v(43.9, 120.25) * mm, "radius": 3.18 * mm});
            skCircle(sketch, "E5.13.16.0", {"center": v(51.7, 142.75) * mm, "radius": 3.18 * mm});
            skCircle(sketch, "E5.13.16.1", {"center": v(43.9, 129.25) * mm, "radius": 3.18 * mm});
            skCircle(sketch, "E5.13.16.2", {"center": v(51.7, 133.75) * mm, "radius": 3.18 * mm});
            skCircle(sketch, "E5.13.16.3", {"center": v(43.9, 138.25) * mm, "radius": 3.18 * mm});
            skCircle(sketch, "E5.13.17.0", {"center": v(51.7, 160.75) * mm, "radius": 3.18 * mm});
            skCircle(sketch, "E5.13.17.1", {"center": v(43.9, 147.25) * mm, "radius": 3.18 * mm});
            skCircle(sketch, "E5.13.17.2", {"center": v(51.7, 151.75) * mm, "radius": 3.18 * mm});
            skCircle(sketch, "E5.13.17.3", {"center": v(43.9, 156.25) * mm, "radius": 3.18 * mm});
            skCircle(sketch, "E5.14.0.0", {"center": v(67.28, -145.25) * mm, "radius": 3.18 * mm});
            skCircle(sketch, "E5.14.0.1", {"center": v(59.49, -158.75) * mm, "radius": 3.18 * mm});
            skCircle(sketch, "E5.14.0.2", {"center": v(67.28, -154.25) * mm, "radius": 3.18 * mm});
            skCircle(sketch, "E5.14.0.3", {"center": v(59.49, -149.75) * mm, "radius": 3.18 * mm});
            skCircle(sketch, "E5.14.1.0", {"center": v(67.28, -127.25) * mm, "radius": 3.18 * mm});
            skCircle(sketch, "E5.14.1.1", {"center": v(59.49, -140.75) * mm, "radius": 3.18 * mm});
            skCircle(sketch, "E5.14.1.2", {"center": v(67.28, -136.25) * mm, "radius": 3.18 * mm});
            skCircle(sketch, "E5.14.1.3", {"center": v(59.49, -131.75) * mm, "radius": 3.18 * mm});
            skCircle(sketch, "E5.14.2.0", {"center": v(67.28, -109.25) * mm, "radius": 3.18 * mm});
            skCircle(sketch, "E5.14.2.1", {"center": v(59.49, -122.75) * mm, "radius": 3.18 * mm});
            skCircle(sketch, "E5.14.2.2", {"center": v(67.28, -118.25) * mm, "radius": 3.18 * mm});
            skCircle(sketch, "E5.14.2.3", {"center": v(59.49, -113.75) * mm, "radius": 3.18 * mm});
            skCircle(sketch, "E5.14.3.0", {"center": v(67.28, -91.25) * mm, "radius": 3.18 * mm});
            skCircle(sketch, "E5.14.3.1", {"center": v(59.49, -104.75) * mm, "radius": 3.18 * mm});
            skCircle(sketch, "E5.14.3.2", {"center": v(67.28, -100.25) * mm, "radius": 3.18 * mm});
            skCircle(sketch, "E5.14.3.3", {"center": v(59.49, -95.75) * mm, "radius": 3.18 * mm});
            skCircle(sketch, "E5.14.4.0", {"center": v(67.28, -73.25) * mm, "radius": 3.18 * mm});
            skCircle(sketch, "E5.14.4.1", {"center": v(59.49, -86.75) * mm, "radius": 3.18 * mm});
            skCircle(sketch, "E5.14.4.2", {"center": v(67.28, -82.25) * mm, "radius": 3.18 * mm});
            skCircle(sketch, "E5.14.4.3", {"center": v(59.49, -77.75) * mm, "radius": 3.18 * mm});
            skCircle(sketch, "E5.14.5.0", {"center": v(67.28, -55.25) * mm, "radius": 3.18 * mm});
            skCircle(sketch, "E5.14.5.1", {"center": v(59.49, -68.75) * mm, "radius": 3.18 * mm});
            skCircle(sketch, "E5.14.5.2", {"center": v(67.28, -64.25) * mm, "radius": 3.18 * mm});
            skCircle(sketch, "E5.14.5.3", {"center": v(59.49, -59.75) * mm, "radius": 3.18 * mm});
            skCircle(sketch, "E5.14.6.0", {"center": v(67.28, -37.25) * mm, "radius": 3.18 * mm});
            skCircle(sketch, "E5.14.6.1", {"center": v(59.49, -50.75) * mm, "radius": 3.18 * mm});
            skCircle(sketch, "E5.14.6.2", {"center": v(67.28, -46.25) * mm, "radius": 3.18 * mm});
            skCircle(sketch, "E5.14.6.3", {"center": v(59.49, -41.75) * mm, "radius": 3.18 * mm});
            skCircle(sketch, "E5.14.7.0", {"center": v(67.28, -19.25) * mm, "radius": 3.18 * mm});
            skCircle(sketch, "E5.14.7.1", {"center": v(59.49, -32.75) * mm, "radius": 3.18 * mm});
            skCircle(sketch, "E5.14.7.2", {"center": v(67.28, -28.25) * mm, "radius": 3.18 * mm});
            skCircle(sketch, "E5.14.7.3", {"center": v(59.49, -23.75) * mm, "radius": 3.18 * mm});
            skCircle(sketch, "E5.14.8.0", {"center": v(67.28, -1.25) * mm, "radius": 3.18 * mm});
            skCircle(sketch, "E5.14.8.1", {"center": v(59.49, -14.75) * mm, "radius": 3.18 * mm});
            skCircle(sketch, "E5.14.8.2", {"center": v(67.28, -10.25) * mm, "radius": 3.18 * mm});
            skCircle(sketch, "E5.14.8.3", {"center": v(59.49, -5.75) * mm, "radius": 3.18 * mm});
            skCircle(sketch, "E5.14.9.0", {"center": v(67.28, 16.75) * mm, "radius": 3.18 * mm});
            skCircle(sketch, "E5.14.9.1", {"center": v(59.49, 3.25) * mm, "radius": 3.18 * mm});
            skCircle(sketch, "E5.14.9.2", {"center": v(67.28, 7.75) * mm, "radius": 3.18 * mm});
            skCircle(sketch, "E5.14.9.3", {"center": v(59.49, 12.25) * mm, "radius": 3.18 * mm});
            skCircle(sketch, "E5.14.10.0", {"center": v(67.28, 34.75) * mm, "radius": 3.18 * mm});
            skCircle(sketch, "E5.14.10.1", {"center": v(59.49, 21.25) * mm, "radius": 3.18 * mm});
            skCircle(sketch, "E5.14.10.2", {"center": v(67.28, 25.75) * mm, "radius": 3.18 * mm});
            skCircle(sketch, "E5.14.10.3", {"center": v(59.49, 30.25) * mm, "radius": 3.18 * mm});
            skCircle(sketch, "E5.14.11.0", {"center": v(67.28, 52.75) * mm, "radius": 3.18 * mm});
            skCircle(sketch, "E5.14.11.1", {"center": v(59.49, 39.25) * mm, "radius": 3.18 * mm});
            skCircle(sketch, "E5.14.11.2", {"center": v(67.28, 43.75) * mm, "radius": 3.18 * mm});
            skCircle(sketch, "E5.14.11.3", {"center": v(59.49, 48.25) * mm, "radius": 3.18 * mm});
            skCircle(sketch, "E5.14.12.0", {"center": v(67.28, 70.75) * mm, "radius": 3.18 * mm});
            skCircle(sketch, "E5.14.12.1", {"center": v(59.49, 57.25) * mm, "radius": 3.18 * mm});
            skCircle(sketch, "E5.14.12.2", {"center": v(67.28, 61.75) * mm, "radius": 3.18 * mm});
            skCircle(sketch, "E5.14.12.3", {"center": v(59.49, 66.25) * mm, "radius": 3.18 * mm});
            skCircle(sketch, "E5.14.13.0", {"center": v(67.28, 88.75) * mm, "radius": 3.18 * mm});
            skCircle(sketch, "E5.14.13.1", {"center": v(59.49, 75.25) * mm, "radius": 3.18 * mm});
            skCircle(sketch, "E5.14.13.2", {"center": v(67.28, 79.75) * mm, "radius": 3.18 * mm});
            skCircle(sketch, "E5.14.13.3", {"center": v(59.49, 84.25) * mm, "radius": 3.18 * mm});
            skCircle(sketch, "E5.14.14.0", {"center": v(67.28, 106.75) * mm, "radius": 3.18 * mm});
            skCircle(sketch, "E5.14.14.1", {"center": v(59.49, 93.25) * mm, "radius": 3.18 * mm});
            skCircle(sketch, "E5.14.14.2", {"center": v(67.28, 97.75) * mm, "radius": 3.18 * mm});
            skCircle(sketch, "E5.14.14.3", {"center": v(59.49, 102.25) * mm, "radius": 3.18 * mm});
            skCircle(sketch, "E5.14.15.0", {"center": v(67.28, 124.75) * mm, "radius": 3.18 * mm});
            skCircle(sketch, "E5.14.15.1", {"center": v(59.49, 111.25) * mm, "radius": 3.18 * mm});
            skCircle(sketch, "E5.14.15.2", {"center": v(67.28, 115.75) * mm, "radius": 3.18 * mm});
            skCircle(sketch, "E5.14.15.3", {"center": v(59.49, 120.25) * mm, "radius": 3.18 * mm});
            skCircle(sketch, "E5.14.16.0", {"center": v(67.28, 142.75) * mm, "radius": 3.18 * mm});
            skCircle(sketch, "E5.14.16.1", {"center": v(59.49, 129.25) * mm, "radius": 3.18 * mm});
            skCircle(sketch, "E5.14.16.2", {"center": v(67.28, 133.75) * mm, "radius": 3.18 * mm});
            skCircle(sketch, "E5.14.16.3", {"center": v(59.49, 138.25) * mm, "radius": 3.18 * mm});
            skCircle(sketch, "E5.14.17.0", {"center": v(67.28, 160.75) * mm, "radius": 3.18 * mm});
            skCircle(sketch, "E5.14.17.1", {"center": v(59.49, 147.25) * mm, "radius": 3.18 * mm});
            skCircle(sketch, "E5.14.17.2", {"center": v(67.28, 151.75) * mm, "radius": 3.18 * mm});
            skCircle(sketch, "E5.14.17.3", {"center": v(59.49, 156.25) * mm, "radius": 3.18 * mm});
            skCircle(sketch, "E5.15.0.0", {"center": v(82.87, -145.25) * mm, "radius": 3.18 * mm});
            skCircle(sketch, "E5.15.0.1", {"center": v(75.08, -158.75) * mm, "radius": 3.18 * mm});
            skCircle(sketch, "E5.15.0.2", {"center": v(82.87, -154.25) * mm, "radius": 3.18 * mm});
            skCircle(sketch, "E5.15.0.3", {"center": v(75.08, -149.75) * mm, "radius": 3.18 * mm});
            skCircle(sketch, "E5.15.1.0", {"center": v(82.87, -127.25) * mm, "radius": 3.18 * mm});
            skCircle(sketch, "E5.15.1.1", {"center": v(75.08, -140.75) * mm, "radius": 3.18 * mm});
            skCircle(sketch, "E5.15.1.2", {"center": v(82.87, -136.25) * mm, "radius": 3.18 * mm});
            skCircle(sketch, "E5.15.1.3", {"center": v(75.08, -131.75) * mm, "radius": 3.18 * mm});
            skCircle(sketch, "E5.15.2.0", {"center": v(82.87, -109.25) * mm, "radius": 3.18 * mm});
            skCircle(sketch, "E5.15.2.1", {"center": v(75.08, -122.75) * mm, "radius": 3.18 * mm});
            skCircle(sketch, "E5.15.2.2", {"center": v(82.87, -118.25) * mm, "radius": 3.18 * mm});
            skCircle(sketch, "E5.15.2.3", {"center": v(75.08, -113.75) * mm, "radius": 3.18 * mm});
            skCircle(sketch, "E5.15.3.0", {"center": v(82.87, -91.25) * mm, "radius": 3.18 * mm});
            skCircle(sketch, "E5.15.3.1", {"center": v(75.08, -104.75) * mm, "radius": 3.18 * mm});
            skCircle(sketch, "E5.15.3.2", {"center": v(82.87, -100.25) * mm, "radius": 3.18 * mm});
            skCircle(sketch, "E5.15.3.3", {"center": v(75.08, -95.75) * mm, "radius": 3.18 * mm});
            skCircle(sketch, "E5.15.4.0", {"center": v(82.87, -73.25) * mm, "radius": 3.18 * mm});
            skCircle(sketch, "E5.15.4.1", {"center": v(75.08, -86.75) * mm, "radius": 3.18 * mm});
            skCircle(sketch, "E5.15.4.2", {"center": v(82.87, -82.25) * mm, "radius": 3.18 * mm});
            skCircle(sketch, "E5.15.4.3", {"center": v(75.08, -77.75) * mm, "radius": 3.18 * mm});
            skCircle(sketch, "E5.15.5.0", {"center": v(82.87, -55.25) * mm, "radius": 3.18 * mm});
            skCircle(sketch, "E5.15.5.1", {"center": v(75.08, -68.75) * mm, "radius": 3.18 * mm});
            skCircle(sketch, "E5.15.5.2", {"center": v(82.87, -64.25) * mm, "radius": 3.18 * mm});
            skCircle(sketch, "E5.15.5.3", {"center": v(75.08, -59.75) * mm, "radius": 3.18 * mm});
            skCircle(sketch, "E5.15.6.0", {"center": v(82.87, -37.25) * mm, "radius": 3.18 * mm});
            skCircle(sketch, "E5.15.6.1", {"center": v(75.08, -50.75) * mm, "radius": 3.18 * mm});
            skCircle(sketch, "E5.15.6.2", {"center": v(82.87, -46.25) * mm, "radius": 3.18 * mm});
            skCircle(sketch, "E5.15.6.3", {"center": v(75.08, -41.75) * mm, "radius": 3.18 * mm});
            skCircle(sketch, "E5.15.7.0", {"center": v(82.87, -19.25) * mm, "radius": 3.18 * mm});
            skCircle(sketch, "E5.15.7.1", {"center": v(75.08, -32.75) * mm, "radius": 3.18 * mm});
            skCircle(sketch, "E5.15.7.2", {"center": v(82.87, -28.25) * mm, "radius": 3.18 * mm});
            skCircle(sketch, "E5.15.7.3", {"center": v(75.08, -23.75) * mm, "radius": 3.18 * mm});
            skCircle(sketch, "E5.15.8.0", {"center": v(82.87, -1.25) * mm, "radius": 3.18 * mm});
            skCircle(sketch, "E5.15.8.1", {"center": v(75.08, -14.75) * mm, "radius": 3.18 * mm});
            skCircle(sketch, "E5.15.8.2", {"center": v(82.87, -10.25) * mm, "radius": 3.18 * mm});
            skCircle(sketch, "E5.15.8.3", {"center": v(75.08, -5.75) * mm, "radius": 3.18 * mm});
            skCircle(sketch, "E5.15.9.0", {"center": v(82.87, 16.75) * mm, "radius": 3.18 * mm});
            skCircle(sketch, "E5.15.9.1", {"center": v(75.08, 3.25) * mm, "radius": 3.18 * mm});
            skCircle(sketch, "E5.15.9.2", {"center": v(82.87, 7.75) * mm, "radius": 3.18 * mm});
            skCircle(sketch, "E5.15.9.3", {"center": v(75.08, 12.25) * mm, "radius": 3.18 * mm});
            skCircle(sketch, "E5.15.10.0", {"center": v(82.87, 34.75) * mm, "radius": 3.18 * mm});
            skCircle(sketch, "E5.15.10.1", {"center": v(75.08, 21.25) * mm, "radius": 3.18 * mm});
            skCircle(sketch, "E5.15.10.2", {"center": v(82.87, 25.75) * mm, "radius": 3.18 * mm});
            skCircle(sketch, "E5.15.10.3", {"center": v(75.08, 30.25) * mm, "radius": 3.18 * mm});
            skCircle(sketch, "E5.15.11.0", {"center": v(82.87, 52.75) * mm, "radius": 3.18 * mm});
            skCircle(sketch, "E5.15.11.1", {"center": v(75.08, 39.25) * mm, "radius": 3.18 * mm});
            skCircle(sketch, "E5.15.11.2", {"center": v(82.87, 43.75) * mm, "radius": 3.18 * mm});
            skCircle(sketch, "E5.15.11.3", {"center": v(75.08, 48.25) * mm, "radius": 3.18 * mm});
            skCircle(sketch, "E5.15.12.0", {"center": v(82.87, 70.75) * mm, "radius": 3.18 * mm});
            skCircle(sketch, "E5.15.12.1", {"center": v(75.08, 57.25) * mm, "radius": 3.18 * mm});
            skCircle(sketch, "E5.15.12.2", {"center": v(82.87, 61.75) * mm, "radius": 3.18 * mm});
            skCircle(sketch, "E5.15.12.3", {"center": v(75.08, 66.25) * mm, "radius": 3.18 * mm});
            skCircle(sketch, "E5.15.13.0", {"center": v(82.87, 88.75) * mm, "radius": 3.18 * mm});
            skCircle(sketch, "E5.15.13.1", {"center": v(75.08, 75.25) * mm, "radius": 3.18 * mm});
            skCircle(sketch, "E5.15.13.2", {"center": v(82.87, 79.75) * mm, "radius": 3.18 * mm});
            skCircle(sketch, "E5.15.13.3", {"center": v(75.08, 84.25) * mm, "radius": 3.18 * mm});
            skCircle(sketch, "E5.15.14.0", {"center": v(82.87, 106.75) * mm, "radius": 3.18 * mm});
            skCircle(sketch, "E5.15.14.1", {"center": v(75.08, 93.25) * mm, "radius": 3.18 * mm});
            skCircle(sketch, "E5.15.14.2", {"center": v(82.87, 97.75) * mm, "radius": 3.18 * mm});
            skCircle(sketch, "E5.15.14.3", {"center": v(75.08, 102.25) * mm, "radius": 3.18 * mm});
            skCircle(sketch, "E5.15.15.0", {"center": v(82.87, 124.75) * mm, "radius": 3.18 * mm});
            skCircle(sketch, "E5.15.15.1", {"center": v(75.08, 111.25) * mm, "radius": 3.18 * mm});
            skCircle(sketch, "E5.15.15.2", {"center": v(82.87, 115.75) * mm, "radius": 3.18 * mm});
            skCircle(sketch, "E5.15.15.3", {"center": v(75.08, 120.25) * mm, "radius": 3.18 * mm});
            skCircle(sketch, "E5.15.16.0", {"center": v(82.87, 142.75) * mm, "radius": 3.18 * mm});
            skCircle(sketch, "E5.15.16.1", {"center": v(75.08, 129.25) * mm, "radius": 3.18 * mm});
            skCircle(sketch, "E5.15.16.2", {"center": v(82.87, 133.75) * mm, "radius": 3.18 * mm});
            skCircle(sketch, "E5.15.16.3", {"center": v(75.08, 138.25) * mm, "radius": 3.18 * mm});
            skCircle(sketch, "E5.15.17.0", {"center": v(82.87, 160.75) * mm, "radius": 3.18 * mm});
            skCircle(sketch, "E5.15.17.1", {"center": v(75.08, 147.25) * mm, "radius": 3.18 * mm});
            skCircle(sketch, "E5.15.17.2", {"center": v(82.87, 151.75) * mm, "radius": 3.18 * mm});
            skCircle(sketch, "E5.15.17.3", {"center": v(75.08, 156.25) * mm, "radius": 3.18 * mm});
            skCircle(sketch, "E5.16.0.0", {"center": v(98.46, -145.25) * mm, "radius": 3.18 * mm});
            skCircle(sketch, "E5.16.0.1", {"center": v(90.67, -158.75) * mm, "radius": 3.18 * mm});
            skCircle(sketch, "E5.16.0.2", {"center": v(98.46, -154.25) * mm, "radius": 3.18 * mm});
            skCircle(sketch, "E5.16.0.3", {"center": v(90.67, -149.75) * mm, "radius": 3.18 * mm});
            skCircle(sketch, "E5.16.1.0", {"center": v(98.46, -127.25) * mm, "radius": 3.18 * mm});
            skCircle(sketch, "E5.16.1.1", {"center": v(90.67, -140.75) * mm, "radius": 3.18 * mm});
            skCircle(sketch, "E5.16.1.2", {"center": v(98.46, -136.25) * mm, "radius": 3.18 * mm});
            skCircle(sketch, "E5.16.1.3", {"center": v(90.67, -131.75) * mm, "radius": 3.18 * mm});
            skCircle(sketch, "E5.16.2.0", {"center": v(98.46, -109.25) * mm, "radius": 3.18 * mm});
            skCircle(sketch, "E5.16.2.1", {"center": v(90.67, -122.75) * mm, "radius": 3.18 * mm});
            skCircle(sketch, "E5.16.2.2", {"center": v(98.46, -118.25) * mm, "radius": 3.18 * mm});
            skCircle(sketch, "E5.16.2.3", {"center": v(90.67, -113.75) * mm, "radius": 3.18 * mm});
            skCircle(sketch, "E5.16.3.0", {"center": v(98.46, -91.25) * mm, "radius": 3.18 * mm});
            skCircle(sketch, "E5.16.3.1", {"center": v(90.67, -104.75) * mm, "radius": 3.18 * mm});
            skCircle(sketch, "E5.16.3.2", {"center": v(98.46, -100.25) * mm, "radius": 3.18 * mm});
            skCircle(sketch, "E5.16.3.3", {"center": v(90.67, -95.75) * mm, "radius": 3.18 * mm});
            skCircle(sketch, "E5.16.4.0", {"center": v(98.46, -73.25) * mm, "radius": 3.18 * mm});
            skCircle(sketch, "E5.16.4.1", {"center": v(90.67, -86.75) * mm, "radius": 3.18 * mm});
            skCircle(sketch, "E5.16.4.2", {"center": v(98.46, -82.25) * mm, "radius": 3.18 * mm});
            skCircle(sketch, "E5.16.4.3", {"center": v(90.67, -77.75) * mm, "radius": 3.18 * mm});
            skCircle(sketch, "E5.16.5.0", {"center": v(98.46, -55.25) * mm, "radius": 3.18 * mm});
            skCircle(sketch, "E5.16.5.1", {"center": v(90.67, -68.75) * mm, "radius": 3.18 * mm});
            skCircle(sketch, "E5.16.5.2", {"center": v(98.46, -64.25) * mm, "radius": 3.18 * mm});
            skCircle(sketch, "E5.16.5.3", {"center": v(90.67, -59.75) * mm, "radius": 3.18 * mm});
            skCircle(sketch, "E5.16.6.0", {"center": v(98.46, -37.25) * mm, "radius": 3.18 * mm});
            skCircle(sketch, "E5.16.6.1", {"center": v(90.67, -50.75) * mm, "radius": 3.18 * mm});
            skCircle(sketch, "E5.16.6.2", {"center": v(98.46, -46.25) * mm, "radius": 3.18 * mm});
            skCircle(sketch, "E5.16.6.3", {"center": v(90.67, -41.75) * mm, "radius": 3.18 * mm});
            skCircle(sketch, "E5.16.7.0", {"center": v(98.46, -19.25) * mm, "radius": 3.18 * mm});
            skCircle(sketch, "E5.16.7.1", {"center": v(90.67, -32.75) * mm, "radius": 3.18 * mm});
            skCircle(sketch, "E5.16.7.2", {"center": v(98.46, -28.25) * mm, "radius": 3.18 * mm});
            skCircle(sketch, "E5.16.7.3", {"center": v(90.67, -23.75) * mm, "radius": 3.18 * mm});
            skCircle(sketch, "E5.16.8.0", {"center": v(98.46, -1.25) * mm, "radius": 3.18 * mm});
            skCircle(sketch, "E5.16.8.1", {"center": v(90.67, -14.75) * mm, "radius": 3.18 * mm});
            skCircle(sketch, "E5.16.8.2", {"center": v(98.46, -10.25) * mm, "radius": 3.18 * mm});
            skCircle(sketch, "E5.16.8.3", {"center": v(90.67, -5.75) * mm, "radius": 3.18 * mm});
            skCircle(sketch, "E5.16.9.0", {"center": v(98.46, 16.75) * mm, "radius": 3.18 * mm});
            skCircle(sketch, "E5.16.9.1", {"center": v(90.67, 3.25) * mm, "radius": 3.18 * mm});
            skCircle(sketch, "E5.16.9.2", {"center": v(98.46, 7.75) * mm, "radius": 3.18 * mm});
            skCircle(sketch, "E5.16.9.3", {"center": v(90.67, 12.25) * mm, "radius": 3.18 * mm});
            skCircle(sketch, "E5.16.10.0", {"center": v(98.46, 34.75) * mm, "radius": 3.18 * mm});
            skCircle(sketch, "E5.16.10.1", {"center": v(90.67, 21.25) * mm, "radius": 3.18 * mm});
            skCircle(sketch, "E5.16.10.2", {"center": v(98.46, 25.75) * mm, "radius": 3.18 * mm});
            skCircle(sketch, "E5.16.10.3", {"center": v(90.67, 30.25) * mm, "radius": 3.18 * mm});
            skCircle(sketch, "E5.16.11.0", {"center": v(98.46, 52.75) * mm, "radius": 3.18 * mm});
            skCircle(sketch, "E5.16.11.1", {"center": v(90.67, 39.25) * mm, "radius": 3.18 * mm});
            skCircle(sketch, "E5.16.11.2", {"center": v(98.46, 43.75) * mm, "radius": 3.18 * mm});
            skCircle(sketch, "E5.16.11.3", {"center": v(90.67, 48.25) * mm, "radius": 3.18 * mm});
            skCircle(sketch, "E5.16.12.0", {"center": v(98.46, 70.75) * mm, "radius": 3.18 * mm});
            skCircle(sketch, "E5.16.12.1", {"center": v(90.67, 57.25) * mm, "radius": 3.18 * mm});
            skCircle(sketch, "E5.16.12.2", {"center": v(98.46, 61.75) * mm, "radius": 3.18 * mm});
            skCircle(sketch, "E5.16.12.3", {"center": v(90.67, 66.25) * mm, "radius": 3.18 * mm});
            skCircle(sketch, "E5.16.13.0", {"center": v(98.46, 88.75) * mm, "radius": 3.18 * mm});
            skCircle(sketch, "E5.16.13.1", {"center": v(90.67, 75.25) * mm, "radius": 3.18 * mm});
            skCircle(sketch, "E5.16.13.2", {"center": v(98.46, 79.75) * mm, "radius": 3.18 * mm});
            skCircle(sketch, "E5.16.13.3", {"center": v(90.67, 84.25) * mm, "radius": 3.18 * mm});
            skCircle(sketch, "E5.16.14.0", {"center": v(98.46, 106.75) * mm, "radius": 3.18 * mm});
            skCircle(sketch, "E5.16.14.1", {"center": v(90.67, 93.25) * mm, "radius": 3.18 * mm});
            skCircle(sketch, "E5.16.14.2", {"center": v(98.46, 97.75) * mm, "radius": 3.18 * mm});
            skCircle(sketch, "E5.16.14.3", {"center": v(90.67, 102.25) * mm, "radius": 3.18 * mm});
            skCircle(sketch, "E5.16.15.0", {"center": v(98.46, 124.75) * mm, "radius": 3.18 * mm});
            skCircle(sketch, "E5.16.15.1", {"center": v(90.67, 111.25) * mm, "radius": 3.18 * mm});
            skCircle(sketch, "E5.16.15.2", {"center": v(98.46, 115.75) * mm, "radius": 3.18 * mm});
            skCircle(sketch, "E5.16.15.3", {"center": v(90.67, 120.25) * mm, "radius": 3.18 * mm});
            skCircle(sketch, "E5.16.16.0", {"center": v(98.46, 142.75) * mm, "radius": 3.18 * mm});
            skCircle(sketch, "E5.16.16.1", {"center": v(90.67, 129.25) * mm, "radius": 3.18 * mm});
            skCircle(sketch, "E5.16.16.2", {"center": v(98.46, 133.75) * mm, "radius": 3.18 * mm});
            skCircle(sketch, "E5.16.16.3", {"center": v(90.67, 138.25) * mm, "radius": 3.18 * mm});
            skCircle(sketch, "E5.16.17.0", {"center": v(98.46, 160.75) * mm, "radius": 3.18 * mm});
            skCircle(sketch, "E5.16.17.1", {"center": v(90.67, 147.25) * mm, "radius": 3.18 * mm});
            skCircle(sketch, "E5.16.17.2", {"center": v(98.46, 151.75) * mm, "radius": 3.18 * mm});
            skCircle(sketch, "E5.16.17.3", {"center": v(90.67, 156.25) * mm, "radius": 3.18 * mm});
            skCircle(sketch, "E5.17.0.0", {"center": v(114.05, -145.25) * mm, "radius": 3.18 * mm});
            skCircle(sketch, "E5.17.0.1", {"center": v(106.25, -158.75) * mm, "radius": 3.18 * mm});
            skCircle(sketch, "E5.17.0.2", {"center": v(114.05, -154.25) * mm, "radius": 3.18 * mm});
            skCircle(sketch, "E5.17.0.3", {"center": v(106.25, -149.75) * mm, "radius": 3.18 * mm});
            skCircle(sketch, "E5.17.1.0", {"center": v(114.05, -127.25) * mm, "radius": 3.18 * mm});
            skCircle(sketch, "E5.17.1.1", {"center": v(106.25, -140.75) * mm, "radius": 3.18 * mm});
            skCircle(sketch, "E5.17.1.2", {"center": v(114.05, -136.25) * mm, "radius": 3.18 * mm});
            skCircle(sketch, "E5.17.1.3", {"center": v(106.25, -131.75) * mm, "radius": 3.18 * mm});
            skCircle(sketch, "E5.17.2.0", {"center": v(114.05, -109.25) * mm, "radius": 3.18 * mm});
            skCircle(sketch, "E5.17.2.1", {"center": v(106.25, -122.75) * mm, "radius": 3.18 * mm});
            skCircle(sketch, "E5.17.2.2", {"center": v(114.05, -118.25) * mm, "radius": 3.18 * mm});
            skCircle(sketch, "E5.17.2.3", {"center": v(106.25, -113.75) * mm, "radius": 3.18 * mm});
            skCircle(sketch, "E5.17.3.0", {"center": v(114.05, -91.25) * mm, "radius": 3.18 * mm});
            skCircle(sketch, "E5.17.3.1", {"center": v(106.25, -104.75) * mm, "radius": 3.18 * mm});
            skCircle(sketch, "E5.17.3.2", {"center": v(114.05, -100.25) * mm, "radius": 3.18 * mm});
            skCircle(sketch, "E5.17.3.3", {"center": v(106.25, -95.75) * mm, "radius": 3.18 * mm});
            skCircle(sketch, "E5.17.4.0", {"center": v(114.05, -73.25) * mm, "radius": 3.18 * mm});
            skCircle(sketch, "E5.17.4.1", {"center": v(106.25, -86.75) * mm, "radius": 3.18 * mm});
            skCircle(sketch, "E5.17.4.2", {"center": v(114.05, -82.25) * mm, "radius": 3.18 * mm});
            skCircle(sketch, "E5.17.4.3", {"center": v(106.25, -77.75) * mm, "radius": 3.18 * mm});
            skCircle(sketch, "E5.17.5.0", {"center": v(114.05, -55.25) * mm, "radius": 3.18 * mm});
            skCircle(sketch, "E5.17.5.1", {"center": v(106.25, -68.75) * mm, "radius": 3.18 * mm});
            skCircle(sketch, "E5.17.5.2", {"center": v(114.05, -64.25) * mm, "radius": 3.18 * mm});
            skCircle(sketch, "E5.17.5.3", {"center": v(106.25, -59.75) * mm, "radius": 3.18 * mm});
            skCircle(sketch, "E5.17.6.0", {"center": v(114.05, -37.25) * mm, "radius": 3.18 * mm});
            skCircle(sketch, "E5.17.6.1", {"center": v(106.25, -50.75) * mm, "radius": 3.18 * mm});
            skCircle(sketch, "E5.17.6.2", {"center": v(114.05, -46.25) * mm, "radius": 3.18 * mm});
            skCircle(sketch, "E5.17.6.3", {"center": v(106.25, -41.75) * mm, "radius": 3.18 * mm});
            skCircle(sketch, "E5.17.7.0", {"center": v(114.05, -19.25) * mm, "radius": 3.18 * mm});
            skCircle(sketch, "E5.17.7.1", {"center": v(106.25, -32.75) * mm, "radius": 3.18 * mm});
            skCircle(sketch, "E5.17.7.2", {"center": v(114.05, -28.25) * mm, "radius": 3.18 * mm});
            skCircle(sketch, "E5.17.7.3", {"center": v(106.25, -23.75) * mm, "radius": 3.18 * mm});
            skCircle(sketch, "E5.17.8.0", {"center": v(114.05, -1.25) * mm, "radius": 3.18 * mm});
            skCircle(sketch, "E5.17.8.1", {"center": v(106.25, -14.75) * mm, "radius": 3.18 * mm});
            skCircle(sketch, "E5.17.8.2", {"center": v(114.05, -10.25) * mm, "radius": 3.18 * mm});
            skCircle(sketch, "E5.17.8.3", {"center": v(106.25, -5.75) * mm, "radius": 3.18 * mm});
            skCircle(sketch, "E5.17.9.0", {"center": v(114.05, 16.75) * mm, "radius": 3.18 * mm});
            skCircle(sketch, "E5.17.9.1", {"center": v(106.25, 3.25) * mm, "radius": 3.18 * mm});
            skCircle(sketch, "E5.17.9.2", {"center": v(114.05, 7.75) * mm, "radius": 3.18 * mm});
            skCircle(sketch, "E5.17.9.3", {"center": v(106.25, 12.25) * mm, "radius": 3.18 * mm});
            skCircle(sketch, "E5.17.10.0", {"center": v(114.05, 34.75) * mm, "radius": 3.18 * mm});
            skCircle(sketch, "E5.17.10.1", {"center": v(106.25, 21.25) * mm, "radius": 3.18 * mm});
            skCircle(sketch, "E5.17.10.2", {"center": v(114.05, 25.75) * mm, "radius": 3.18 * mm});
            skCircle(sketch, "E5.17.10.3", {"center": v(106.25, 30.25) * mm, "radius": 3.18 * mm});
            skCircle(sketch, "E5.17.11.0", {"center": v(114.05, 52.75) * mm, "radius": 3.18 * mm});
            skCircle(sketch, "E5.17.11.1", {"center": v(106.25, 39.25) * mm, "radius": 3.18 * mm});
            skCircle(sketch, "E5.17.11.2", {"center": v(114.05, 43.75) * mm, "radius": 3.18 * mm});
            skCircle(sketch, "E5.17.11.3", {"center": v(106.25, 48.25) * mm, "radius": 3.18 * mm});
            skCircle(sketch, "E5.17.12.0", {"center": v(114.05, 70.75) * mm, "radius": 3.18 * mm});
            skCircle(sketch, "E5.17.12.1", {"center": v(106.25, 57.25) * mm, "radius": 3.18 * mm});
            skCircle(sketch, "E5.17.12.2", {"center": v(114.05, 61.75) * mm, "radius": 3.18 * mm});
            skCircle(sketch, "E5.17.12.3", {"center": v(106.25, 66.25) * mm, "radius": 3.18 * mm});
            skCircle(sketch, "E5.17.13.0", {"center": v(114.05, 88.75) * mm, "radius": 3.18 * mm});
            skCircle(sketch, "E5.17.13.1", {"center": v(106.25, 75.25) * mm, "radius": 3.18 * mm});
            skCircle(sketch, "E5.17.13.2", {"center": v(114.05, 79.75) * mm, "radius": 3.18 * mm});
            skCircle(sketch, "E5.17.13.3", {"center": v(106.25, 84.25) * mm, "radius": 3.18 * mm});
            skCircle(sketch, "E5.17.14.0", {"center": v(114.05, 106.75) * mm, "radius": 3.18 * mm});
            skCircle(sketch, "E5.17.14.1", {"center": v(106.25, 93.25) * mm, "radius": 3.18 * mm});
            skCircle(sketch, "E5.17.14.2", {"center": v(114.05, 97.75) * mm, "radius": 3.18 * mm});
            skCircle(sketch, "E5.17.14.3", {"center": v(106.25, 102.25) * mm, "radius": 3.18 * mm});
            skCircle(sketch, "E5.17.15.0", {"center": v(114.05, 124.75) * mm, "radius": 3.18 * mm});
            skCircle(sketch, "E5.17.15.1", {"center": v(106.25, 111.25) * mm, "radius": 3.18 * mm});
            skCircle(sketch, "E5.17.15.2", {"center": v(114.05, 115.75) * mm, "radius": 3.18 * mm});
            skCircle(sketch, "E5.17.15.3", {"center": v(106.25, 120.25) * mm, "radius": 3.18 * mm});
            skCircle(sketch, "E5.17.16.0", {"center": v(114.05, 142.75) * mm, "radius": 3.18 * mm});
            skCircle(sketch, "E5.17.16.1", {"center": v(106.25, 129.25) * mm, "radius": 3.18 * mm});
            skCircle(sketch, "E5.17.16.2", {"center": v(114.05, 133.75) * mm, "radius": 3.18 * mm});
            skCircle(sketch, "E5.17.16.3", {"center": v(106.25, 138.25) * mm, "radius": 3.18 * mm});
            skCircle(sketch, "E5.17.17.0", {"center": v(114.05, 160.75) * mm, "radius": 3.18 * mm});
            skCircle(sketch, "E5.17.17.1", {"center": v(106.25, 147.25) * mm, "radius": 3.18 * mm});
            skCircle(sketch, "E5.17.17.2", {"center": v(114.05, 151.75) * mm, "radius": 3.18 * mm});
            skCircle(sketch, "E5.17.17.3", {"center": v(106.25, 156.25) * mm, "radius": 3.18 * mm});
            skCircle(sketch, "E5.18.0.0", {"center": v(129.64, -145.25) * mm, "radius": 3.18 * mm});
            skCircle(sketch, "E5.18.0.1", {"center": v(121.84, -158.75) * mm, "radius": 3.18 * mm});
            skCircle(sketch, "E5.18.0.2", {"center": v(129.64, -154.25) * mm, "radius": 3.18 * mm});
            skCircle(sketch, "E5.18.0.3", {"center": v(121.84, -149.75) * mm, "radius": 3.18 * mm});
            skCircle(sketch, "E5.18.1.0", {"center": v(129.64, -127.25) * mm, "radius": 3.18 * mm});
            skCircle(sketch, "E5.18.1.1", {"center": v(121.84, -140.75) * mm, "radius": 3.18 * mm});
            skCircle(sketch, "E5.18.1.2", {"center": v(129.64, -136.25) * mm, "radius": 3.18 * mm});
            skCircle(sketch, "E5.18.1.3", {"center": v(121.84, -131.75) * mm, "radius": 3.18 * mm});
            skCircle(sketch, "E5.18.2.0", {"center": v(129.64, -109.25) * mm, "radius": 3.18 * mm});
            skCircle(sketch, "E5.18.2.1", {"center": v(121.84, -122.75) * mm, "radius": 3.18 * mm});
            skCircle(sketch, "E5.18.2.2", {"center": v(129.64, -118.25) * mm, "radius": 3.18 * mm});
            skCircle(sketch, "E5.18.2.3", {"center": v(121.84, -113.75) * mm, "radius": 3.18 * mm});
            skCircle(sketch, "E5.18.3.0", {"center": v(129.64, -91.25) * mm, "radius": 3.18 * mm});
            skCircle(sketch, "E5.18.3.1", {"center": v(121.84, -104.75) * mm, "radius": 3.18 * mm});
            skCircle(sketch, "E5.18.3.2", {"center": v(129.64, -100.25) * mm, "radius": 3.18 * mm});
            skCircle(sketch, "E5.18.3.3", {"center": v(121.84, -95.75) * mm, "radius": 3.18 * mm});
            skCircle(sketch, "E5.18.4.0", {"center": v(129.64, -73.25) * mm, "radius": 3.18 * mm});
            skCircle(sketch, "E5.18.4.1", {"center": v(121.84, -86.75) * mm, "radius": 3.18 * mm});
            skCircle(sketch, "E5.18.4.2", {"center": v(129.64, -82.25) * mm, "radius": 3.18 * mm});
            skCircle(sketch, "E5.18.4.3", {"center": v(121.84, -77.75) * mm, "radius": 3.18 * mm});
            skCircle(sketch, "E5.18.5.0", {"center": v(129.64, -55.25) * mm, "radius": 3.18 * mm});
            skCircle(sketch, "E5.18.5.1", {"center": v(121.84, -68.75) * mm, "radius": 3.18 * mm});
            skCircle(sketch, "E5.18.5.2", {"center": v(129.64, -64.25) * mm, "radius": 3.18 * mm});
            skCircle(sketch, "E5.18.5.3", {"center": v(121.84, -59.75) * mm, "radius": 3.18 * mm});
            skCircle(sketch, "E5.18.6.0", {"center": v(129.64, -37.25) * mm, "radius": 3.18 * mm});
            skCircle(sketch, "E5.18.6.1", {"center": v(121.84, -50.75) * mm, "radius": 3.18 * mm});
            skCircle(sketch, "E5.18.6.2", {"center": v(129.64, -46.25) * mm, "radius": 3.18 * mm});
            skCircle(sketch, "E5.18.6.3", {"center": v(121.84, -41.75) * mm, "radius": 3.18 * mm});
            skCircle(sketch, "E5.18.7.0", {"center": v(129.64, -19.25) * mm, "radius": 3.18 * mm});
            skCircle(sketch, "E5.18.7.1", {"center": v(121.84, -32.75) * mm, "radius": 3.18 * mm});
            skCircle(sketch, "E5.18.7.2", {"center": v(129.64, -28.25) * mm, "radius": 3.18 * mm});
            skCircle(sketch, "E5.18.7.3", {"center": v(121.84, -23.75) * mm, "radius": 3.18 * mm});
            skCircle(sketch, "E5.18.8.0", {"center": v(129.64, -1.25) * mm, "radius": 3.18 * mm});
            skCircle(sketch, "E5.18.8.1", {"center": v(121.84, -14.75) * mm, "radius": 3.18 * mm});
            skCircle(sketch, "E5.18.8.2", {"center": v(129.64, -10.25) * mm, "radius": 3.18 * mm});
            skCircle(sketch, "E5.18.8.3", {"center": v(121.84, -5.75) * mm, "radius": 3.18 * mm});
            skCircle(sketch, "E5.18.9.0", {"center": v(129.64, 16.75) * mm, "radius": 3.18 * mm});
            skCircle(sketch, "E5.18.9.1", {"center": v(121.84, 3.25) * mm, "radius": 3.18 * mm});
            skCircle(sketch, "E5.18.9.2", {"center": v(129.64, 7.75) * mm, "radius": 3.18 * mm});
            skCircle(sketch, "E5.18.9.3", {"center": v(121.84, 12.25) * mm, "radius": 3.18 * mm});
            skCircle(sketch, "E5.18.10.0", {"center": v(129.64, 34.75) * mm, "radius": 3.18 * mm});
            skCircle(sketch, "E5.18.10.1", {"center": v(121.84, 21.25) * mm, "radius": 3.18 * mm});
            skCircle(sketch, "E5.18.10.2", {"center": v(129.64, 25.75) * mm, "radius": 3.18 * mm});
            skCircle(sketch, "E5.18.10.3", {"center": v(121.84, 30.25) * mm, "radius": 3.18 * mm});
            skCircle(sketch, "E5.18.11.0", {"center": v(129.64, 52.75) * mm, "radius": 3.18 * mm});
            skCircle(sketch, "E5.18.11.1", {"center": v(121.84, 39.25) * mm, "radius": 3.18 * mm});
            skCircle(sketch, "E5.18.11.2", {"center": v(129.64, 43.75) * mm, "radius": 3.18 * mm});
            skCircle(sketch, "E5.18.11.3", {"center": v(121.84, 48.25) * mm, "radius": 3.18 * mm});
            skCircle(sketch, "E5.18.12.0", {"center": v(129.64, 70.75) * mm, "radius": 3.18 * mm});
            skCircle(sketch, "E5.18.12.1", {"center": v(121.84, 57.25) * mm, "radius": 3.18 * mm});
            skCircle(sketch, "E5.18.12.2", {"center": v(129.64, 61.75) * mm, "radius": 3.18 * mm});
            skCircle(sketch, "E5.18.12.3", {"center": v(121.84, 66.25) * mm, "radius": 3.18 * mm});
            skCircle(sketch, "E5.18.13.0", {"center": v(129.64, 88.75) * mm, "radius": 3.18 * mm});
            skCircle(sketch, "E5.18.13.1", {"center": v(121.84, 75.25) * mm, "radius": 3.18 * mm});
            skCircle(sketch, "E5.18.13.2", {"center": v(129.64, 79.75) * mm, "radius": 3.18 * mm});
            skCircle(sketch, "E5.18.13.3", {"center": v(121.84, 84.25) * mm, "radius": 3.18 * mm});
            skCircle(sketch, "E5.18.14.0", {"center": v(129.64, 106.75) * mm, "radius": 3.18 * mm});
            skCircle(sketch, "E5.18.14.1", {"center": v(121.84, 93.25) * mm, "radius": 3.18 * mm});
            skCircle(sketch, "E5.18.14.2", {"center": v(129.64, 97.75) * mm, "radius": 3.18 * mm});
            skCircle(sketch, "E5.18.14.3", {"center": v(121.84, 102.25) * mm, "radius": 3.18 * mm});
            skCircle(sketch, "E5.18.15.0", {"center": v(129.64, 124.75) * mm, "radius": 3.18 * mm});
            skCircle(sketch, "E5.18.15.1", {"center": v(121.84, 111.25) * mm, "radius": 3.18 * mm});
            skCircle(sketch, "E5.18.15.2", {"center": v(129.64, 115.75) * mm, "radius": 3.18 * mm});
            skCircle(sketch, "E5.18.15.3", {"center": v(121.84, 120.25) * mm, "radius": 3.18 * mm});
            skCircle(sketch, "E5.18.16.0", {"center": v(129.64, 142.75) * mm, "radius": 3.18 * mm});
            skCircle(sketch, "E5.18.16.1", {"center": v(121.84, 129.25) * mm, "radius": 3.18 * mm});
            skCircle(sketch, "E5.18.16.2", {"center": v(129.64, 133.75) * mm, "radius": 3.18 * mm});
            skCircle(sketch, "E5.18.16.3", {"center": v(121.84, 138.25) * mm, "radius": 3.18 * mm});
            skCircle(sketch, "E5.18.17.0", {"center": v(129.64, 160.75) * mm, "radius": 3.18 * mm});
            skCircle(sketch, "E5.18.17.1", {"center": v(121.84, 147.25) * mm, "radius": 3.18 * mm});
            skCircle(sketch, "E5.18.17.2", {"center": v(129.64, 151.75) * mm, "radius": 3.18 * mm});
            skCircle(sketch, "E5.18.17.3", {"center": v(121.84, 156.25) * mm, "radius": 3.18 * mm});
            skCircle(sketch, "E5.19.0.0", {"center": v(145.22, -145.25) * mm, "radius": 3.18 * mm});
            skCircle(sketch, "E5.19.0.1", {"center": v(137.43, -158.75) * mm, "radius": 3.18 * mm});
            skCircle(sketch, "E5.19.0.2", {"center": v(145.22, -154.25) * mm, "radius": 3.18 * mm});
            skCircle(sketch, "E5.19.0.3", {"center": v(137.43, -149.75) * mm, "radius": 3.18 * mm});
            skCircle(sketch, "E5.19.1.0", {"center": v(145.22, -127.25) * mm, "radius": 3.18 * mm});
            skCircle(sketch, "E5.19.1.1", {"center": v(137.43, -140.75) * mm, "radius": 3.18 * mm});
            skCircle(sketch, "E5.19.1.2", {"center": v(145.22, -136.25) * mm, "radius": 3.18 * mm});
            skCircle(sketch, "E5.19.1.3", {"center": v(137.43, -131.75) * mm, "radius": 3.18 * mm});
            skCircle(sketch, "E5.19.2.0", {"center": v(145.22, -109.25) * mm, "radius": 3.18 * mm});
            skCircle(sketch, "E5.19.2.1", {"center": v(137.43, -122.75) * mm, "radius": 3.18 * mm});
            skCircle(sketch, "E5.19.2.2", {"center": v(145.22, -118.25) * mm, "radius": 3.18 * mm});
            skCircle(sketch, "E5.19.2.3", {"center": v(137.43, -113.75) * mm, "radius": 3.18 * mm});
            skCircle(sketch, "E5.19.3.0", {"center": v(145.22, -91.25) * mm, "radius": 3.18 * mm});
            skCircle(sketch, "E5.19.3.1", {"center": v(137.43, -104.75) * mm, "radius": 3.18 * mm});
            skCircle(sketch, "E5.19.3.2", {"center": v(145.22, -100.25) * mm, "radius": 3.18 * mm});
            skCircle(sketch, "E5.19.3.3", {"center": v(137.43, -95.75) * mm, "radius": 3.18 * mm});
            skCircle(sketch, "E5.19.4.0", {"center": v(145.22, -73.25) * mm, "radius": 3.18 * mm});
            skCircle(sketch, "E5.19.4.1", {"center": v(137.43, -86.75) * mm, "radius": 3.18 * mm});
            skCircle(sketch, "E5.19.4.2", {"center": v(145.22, -82.25) * mm, "radius": 3.18 * mm});
            skCircle(sketch, "E5.19.4.3", {"center": v(137.43, -77.75) * mm, "radius": 3.18 * mm});
            skCircle(sketch, "E5.19.5.0", {"center": v(145.22, -55.25) * mm, "radius": 3.18 * mm});
            skCircle(sketch, "E5.19.5.1", {"center": v(137.43, -68.75) * mm, "radius": 3.18 * mm});
            skCircle(sketch, "E5.19.5.2", {"center": v(145.22, -64.25) * mm, "radius": 3.18 * mm});
            skCircle(sketch, "E5.19.5.3", {"center": v(137.43, -59.75) * mm, "radius": 3.18 * mm});
            skCircle(sketch, "E5.19.6.0", {"center": v(145.22, -37.25) * mm, "radius": 3.18 * mm});
            skCircle(sketch, "E5.19.6.1", {"center": v(137.43, -50.75) * mm, "radius": 3.18 * mm});
            skCircle(sketch, "E5.19.6.2", {"center": v(145.22, -46.25) * mm, "radius": 3.18 * mm});
            skCircle(sketch, "E5.19.6.3", {"center": v(137.43, -41.75) * mm, "radius": 3.18 * mm});
            skCircle(sketch, "E5.19.7.0", {"center": v(145.22, -19.25) * mm, "radius": 3.18 * mm});
            skCircle(sketch, "E5.19.7.1", {"center": v(137.43, -32.75) * mm, "radius": 3.18 * mm});
            skCircle(sketch, "E5.19.7.2", {"center": v(145.22, -28.25) * mm, "radius": 3.18 * mm});
            skCircle(sketch, "E5.19.7.3", {"center": v(137.43, -23.75) * mm, "radius": 3.18 * mm});
            skCircle(sketch, "E5.19.8.0", {"center": v(145.22, -1.25) * mm, "radius": 3.18 * mm});
            skCircle(sketch, "E5.19.8.1", {"center": v(137.43, -14.75) * mm, "radius": 3.18 * mm});
            skCircle(sketch, "E5.19.8.2", {"center": v(145.22, -10.25) * mm, "radius": 3.18 * mm});
            skCircle(sketch, "E5.19.8.3", {"center": v(137.43, -5.75) * mm, "radius": 3.18 * mm});
            skCircle(sketch, "E5.19.9.0", {"center": v(145.22, 16.75) * mm, "radius": 3.18 * mm});
            skCircle(sketch, "E5.19.9.1", {"center": v(137.43, 3.25) * mm, "radius": 3.18 * mm});
            skCircle(sketch, "E5.19.9.2", {"center": v(145.22, 7.75) * mm, "radius": 3.18 * mm});
            skCircle(sketch, "E5.19.9.3", {"center": v(137.43, 12.25) * mm, "radius": 3.18 * mm});
            skCircle(sketch, "E5.19.10.0", {"center": v(145.22, 34.75) * mm, "radius": 3.18 * mm});
            skCircle(sketch, "E5.19.10.1", {"center": v(137.43, 21.25) * mm, "radius": 3.18 * mm});
            skCircle(sketch, "E5.19.10.2", {"center": v(145.22, 25.75) * mm, "radius": 3.18 * mm});
            skCircle(sketch, "E5.19.10.3", {"center": v(137.43, 30.25) * mm, "radius": 3.18 * mm});
            skCircle(sketch, "E5.19.11.0", {"center": v(145.22, 52.75) * mm, "radius": 3.18 * mm});
            skCircle(sketch, "E5.19.11.1", {"center": v(137.43, 39.25) * mm, "radius": 3.18 * mm});
            skCircle(sketch, "E5.19.11.2", {"center": v(145.22, 43.75) * mm, "radius": 3.18 * mm});
            skCircle(sketch, "E5.19.11.3", {"center": v(137.43, 48.25) * mm, "radius": 3.18 * mm});
            skCircle(sketch, "E5.19.12.0", {"center": v(145.22, 70.75) * mm, "radius": 3.18 * mm});
            skCircle(sketch, "E5.19.12.1", {"center": v(137.43, 57.25) * mm, "radius": 3.18 * mm});
            skCircle(sketch, "E5.19.12.2", {"center": v(145.22, 61.75) * mm, "radius": 3.18 * mm});
            skCircle(sketch, "E5.19.12.3", {"center": v(137.43, 66.25) * mm, "radius": 3.18 * mm});
            skCircle(sketch, "E5.19.13.0", {"center": v(145.22, 88.75) * mm, "radius": 3.18 * mm});
            skCircle(sketch, "E5.19.13.1", {"center": v(137.43, 75.25) * mm, "radius": 3.18 * mm});
            skCircle(sketch, "E5.19.13.2", {"center": v(145.22, 79.75) * mm, "radius": 3.18 * mm});
            skCircle(sketch, "E5.19.13.3", {"center": v(137.43, 84.25) * mm, "radius": 3.18 * mm});
            skCircle(sketch, "E5.19.14.0", {"center": v(145.22, 106.75) * mm, "radius": 3.18 * mm});
            skCircle(sketch, "E5.19.14.1", {"center": v(137.43, 93.25) * mm, "radius": 3.18 * mm});
            skCircle(sketch, "E5.19.14.2", {"center": v(145.22, 97.75) * mm, "radius": 3.18 * mm});
            skCircle(sketch, "E5.19.14.3", {"center": v(137.43, 102.25) * mm, "radius": 3.18 * mm});
            skCircle(sketch, "E5.19.15.0", {"center": v(145.22, 124.75) * mm, "radius": 3.18 * mm});
            skCircle(sketch, "E5.19.15.1", {"center": v(137.43, 111.25) * mm, "radius": 3.18 * mm});
            skCircle(sketch, "E5.19.15.2", {"center": v(145.22, 115.75) * mm, "radius": 3.18 * mm});
            skCircle(sketch, "E5.19.15.3", {"center": v(137.43, 120.25) * mm, "radius": 3.18 * mm});
            skCircle(sketch, "E5.19.16.0", {"center": v(145.22, 142.75) * mm, "radius": 3.18 * mm});
            skCircle(sketch, "E5.19.16.1", {"center": v(137.43, 129.25) * mm, "radius": 3.18 * mm});
            skCircle(sketch, "E5.19.16.2", {"center": v(145.22, 133.75) * mm, "radius": 3.18 * mm});
            skCircle(sketch, "E5.19.16.3", {"center": v(137.43, 138.25) * mm, "radius": 3.18 * mm});
            skCircle(sketch, "E5.19.17.0", {"center": v(145.22, 160.75) * mm, "radius": 3.18 * mm});
            skCircle(sketch, "E5.19.17.1", {"center": v(137.43, 147.25) * mm, "radius": 3.18 * mm});
            skCircle(sketch, "E5.19.17.2", {"center": v(145.22, 151.75) * mm, "radius": 3.18 * mm});
            skCircle(sketch, "E5.19.17.3", {"center": v(137.43, 156.25) * mm, "radius": 3.18 * mm});
            skCircle(sketch, "E5.20.0.0", {"center": v(160.81, -145.25) * mm, "radius": 3.18 * mm});
            skCircle(sketch, "E5.20.0.1", {"center": v(153.02, -158.75) * mm, "radius": 3.18 * mm});
            skCircle(sketch, "E5.20.0.2", {"center": v(160.81, -154.25) * mm, "radius": 3.18 * mm});
            skCircle(sketch, "E5.20.0.3", {"center": v(153.02, -149.75) * mm, "radius": 3.18 * mm});
            skCircle(sketch, "E5.20.1.0", {"center": v(160.81, -127.25) * mm, "radius": 3.18 * mm});
            skCircle(sketch, "E5.20.1.1", {"center": v(153.02, -140.75) * mm, "radius": 3.18 * mm});
            skCircle(sketch, "E5.20.1.2", {"center": v(160.81, -136.25) * mm, "radius": 3.18 * mm});
            skCircle(sketch, "E5.20.1.3", {"center": v(153.02, -131.75) * mm, "radius": 3.18 * mm});
            skCircle(sketch, "E5.20.2.0", {"center": v(160.81, -109.25) * mm, "radius": 3.18 * mm});
            skCircle(sketch, "E5.20.2.1", {"center": v(153.02, -122.75) * mm, "radius": 3.18 * mm});
            skCircle(sketch, "E5.20.2.2", {"center": v(160.81, -118.25) * mm, "radius": 3.18 * mm});
            skCircle(sketch, "E5.20.2.3", {"center": v(153.02, -113.75) * mm, "radius": 3.18 * mm});
            skCircle(sketch, "E5.20.3.0", {"center": v(160.81, -91.25) * mm, "radius": 3.18 * mm});
            skCircle(sketch, "E5.20.3.1", {"center": v(153.02, -104.75) * mm, "radius": 3.18 * mm});
            skCircle(sketch, "E5.20.3.2", {"center": v(160.81, -100.25) * mm, "radius": 3.18 * mm});
            skCircle(sketch, "E5.20.3.3", {"center": v(153.02, -95.75) * mm, "radius": 3.18 * mm});
            skCircle(sketch, "E5.20.4.0", {"center": v(160.81, -73.25) * mm, "radius": 3.18 * mm});
            skCircle(sketch, "E5.20.4.1", {"center": v(153.02, -86.75) * mm, "radius": 3.18 * mm});
            skCircle(sketch, "E5.20.4.2", {"center": v(160.81, -82.25) * mm, "radius": 3.18 * mm});
            skCircle(sketch, "E5.20.4.3", {"center": v(153.02, -77.75) * mm, "radius": 3.18 * mm});
            skCircle(sketch, "E5.20.5.0", {"center": v(160.81, -55.25) * mm, "radius": 3.18 * mm});
            skCircle(sketch, "E5.20.5.1", {"center": v(153.02, -68.75) * mm, "radius": 3.18 * mm});
            skCircle(sketch, "E5.20.5.2", {"center": v(160.81, -64.25) * mm, "radius": 3.18 * mm});
            skCircle(sketch, "E5.20.5.3", {"center": v(153.02, -59.75) * mm, "radius": 3.18 * mm});
            skCircle(sketch, "E5.20.6.0", {"center": v(160.81, -37.25) * mm, "radius": 3.18 * mm});
            skCircle(sketch, "E5.20.6.1", {"center": v(153.02, -50.75) * mm, "radius": 3.18 * mm});
            skCircle(sketch, "E5.20.6.2", {"center": v(160.81, -46.25) * mm, "radius": 3.18 * mm});
            skCircle(sketch, "E5.20.6.3", {"center": v(153.02, -41.75) * mm, "radius": 3.18 * mm});
            skCircle(sketch, "E5.20.7.0", {"center": v(160.81, -19.25) * mm, "radius": 3.18 * mm});
            skCircle(sketch, "E5.20.7.1", {"center": v(153.02, -32.75) * mm, "radius": 3.18 * mm});
            skCircle(sketch, "E5.20.7.2", {"center": v(160.81, -28.25) * mm, "radius": 3.18 * mm});
            skCircle(sketch, "E5.20.7.3", {"center": v(153.02, -23.75) * mm, "radius": 3.18 * mm});
            skCircle(sketch, "E5.20.8.0", {"center": v(160.81, -1.25) * mm, "radius": 3.18 * mm});
            skCircle(sketch, "E5.20.8.1", {"center": v(153.02, -14.75) * mm, "radius": 3.18 * mm});
            skCircle(sketch, "E5.20.8.2", {"center": v(160.81, -10.25) * mm, "radius": 3.18 * mm});
            skCircle(sketch, "E5.20.8.3", {"center": v(153.02, -5.75) * mm, "radius": 3.18 * mm});
            skCircle(sketch, "E5.20.9.0", {"center": v(160.81, 16.75) * mm, "radius": 3.18 * mm});
            skCircle(sketch, "E5.20.9.1", {"center": v(153.02, 3.25) * mm, "radius": 3.18 * mm});
            skCircle(sketch, "E5.20.9.2", {"center": v(160.81, 7.75) * mm, "radius": 3.18 * mm});
            skCircle(sketch, "E5.20.9.3", {"center": v(153.02, 12.25) * mm, "radius": 3.18 * mm});
            skCircle(sketch, "E5.20.10.0", {"center": v(160.81, 34.75) * mm, "radius": 3.18 * mm});
            skCircle(sketch, "E5.20.10.1", {"center": v(153.02, 21.25) * mm, "radius": 3.18 * mm});
            skCircle(sketch, "E5.20.10.2", {"center": v(160.81, 25.75) * mm, "radius": 3.18 * mm});
            skCircle(sketch, "E5.20.10.3", {"center": v(153.02, 30.25) * mm, "radius": 3.18 * mm});
            skCircle(sketch, "E5.20.11.0", {"center": v(160.81, 52.75) * mm, "radius": 3.18 * mm});
            skCircle(sketch, "E5.20.11.1", {"center": v(153.02, 39.25) * mm, "radius": 3.18 * mm});
            skCircle(sketch, "E5.20.11.2", {"center": v(160.81, 43.75) * mm, "radius": 3.18 * mm});
            skCircle(sketch, "E5.20.11.3", {"center": v(153.02, 48.25) * mm, "radius": 3.18 * mm});
            skCircle(sketch, "E5.20.12.0", {"center": v(160.81, 70.75) * mm, "radius": 3.18 * mm});
            skCircle(sketch, "E5.20.12.1", {"center": v(153.02, 57.25) * mm, "radius": 3.18 * mm});
            skCircle(sketch, "E5.20.12.2", {"center": v(160.81, 61.75) * mm, "radius": 3.18 * mm});
            skCircle(sketch, "E5.20.12.3", {"center": v(153.02, 66.25) * mm, "radius": 3.18 * mm});
            skCircle(sketch, "E5.20.13.0", {"center": v(160.81, 88.75) * mm, "radius": 3.18 * mm});
            skCircle(sketch, "E5.20.13.1", {"center": v(153.02, 75.25) * mm, "radius": 3.18 * mm});
            skCircle(sketch, "E5.20.13.2", {"center": v(160.81, 79.75) * mm, "radius": 3.18 * mm});
            skCircle(sketch, "E5.20.13.3", {"center": v(153.02, 84.25) * mm, "radius": 3.18 * mm});
            skCircle(sketch, "E5.20.14.0", {"center": v(160.81, 106.75) * mm, "radius": 3.18 * mm});
            skCircle(sketch, "E5.20.14.1", {"center": v(153.02, 93.25) * mm, "radius": 3.18 * mm});
            skCircle(sketch, "E5.20.14.2", {"center": v(160.81, 97.75) * mm, "radius": 3.18 * mm});
            skCircle(sketch, "E5.20.14.3", {"center": v(153.02, 102.25) * mm, "radius": 3.18 * mm});
            skCircle(sketch, "E5.20.15.0", {"center": v(160.81, 124.75) * mm, "radius": 3.18 * mm});
            skCircle(sketch, "E5.20.15.1", {"center": v(153.02, 111.25) * mm, "radius": 3.18 * mm});
            skCircle(sketch, "E5.20.15.2", {"center": v(160.81, 115.75) * mm, "radius": 3.18 * mm});
            skCircle(sketch, "E5.20.15.3", {"center": v(153.02, 120.25) * mm, "radius": 3.18 * mm});
            skCircle(sketch, "E5.20.16.0", {"center": v(160.81, 142.75) * mm, "radius": 3.18 * mm});
            skCircle(sketch, "E5.20.16.1", {"center": v(153.02, 129.25) * mm, "radius": 3.18 * mm});
            skCircle(sketch, "E5.20.16.2", {"center": v(160.81, 133.75) * mm, "radius": 3.18 * mm});
            skCircle(sketch, "E5.20.16.3", {"center": v(153.02, 138.25) * mm, "radius": 3.18 * mm});
            skCircle(sketch, "E5.20.17.0", {"center": v(160.81, 160.75) * mm, "radius": 3.18 * mm});
            skCircle(sketch, "E5.20.17.1", {"center": v(153.02, 147.25) * mm, "radius": 3.18 * mm});
            skCircle(sketch, "E5.20.17.2", {"center": v(160.81, 151.75) * mm, "radius": 3.18 * mm});
            skCircle(sketch, "E5.20.17.3", {"center": v(153.02, 156.25) * mm, "radius": 3.18 * mm});
            skLineSegment(sketch, "E5.direction1", {"start": v(-158.75, -158.75) * mm, "end": v(-143.16, -158.75) * mm, "construction": true});
            skLineSegment(sketch, "E5.direction2", {"start": v(-158.75, -158.75) * mm, "end": v(-158.75, -140.75) * mm, "construction": true});
            skCircle(sketch, "E6", {"center": v(-2.87, 3.25) * mm, "radius": 152.4 * mm});
            skCircle(sketch, "E7", {"center": v(-2.87, 3.25) * mm, "radius": 158.75 * mm});
            skSolve(sketch);
        }
        {
            var Q0;
            Q0=makeQuery(id+"F0.imprint","IMPRINT",FACE,{"disambiguationData":[TD([[makeQuery(id+"F0.imprint","IMPRINT",EDGE,{"derivedFrom":sQuery(id+"F0.wireOp",EDGE,"E5.0.8.0")}),-1.0]])]});
            extrude(context, id + "F1", {"entities" : qUnion([Q0]), "depth" : 25 * mm, "offsetDistance" : 25 * mm});
        }
        {
            var Q0;
            Q0=makeQuery(id+"F0.imprint","IMPRINT",FACE,{"disambiguationData":[TD([[makeQuery(id+"F0.imprint","IMPRINT",EDGE,{"derivedFrom":sQuery(id+"F0.wireOp",EDGE,"E5.0.8.0")}),-1.0]])]});
            var sketch = newSketch(context, id + "F2", { "sketchPlane" : qUnion([Q0])});
            skCircle(sketch, "E8", {"center": v(-2.87, 3.25) * mm, "radius": 158.75 * mm});
            skSolve(sketch);
        }
        {
            var Q0;
            Q0=makeQuery(id+"F2.imprint","IMPRINT",FACE,{"disambiguationData":[TD([[makeQuery(id+"F2.imprint","IMPRINT",EDGE,{"derivedFrom":sQuery(id+"F2.wireOp",EDGE,"E8")}),1.0]])]});
            extrude(context, id + "F3", {"entities" : qUnion([Q0]), "operationType" : NewBodyOperationType.ADD, "depth" : 25 * mm, "offsetDistance" : 25 * mm});
        }
    });
